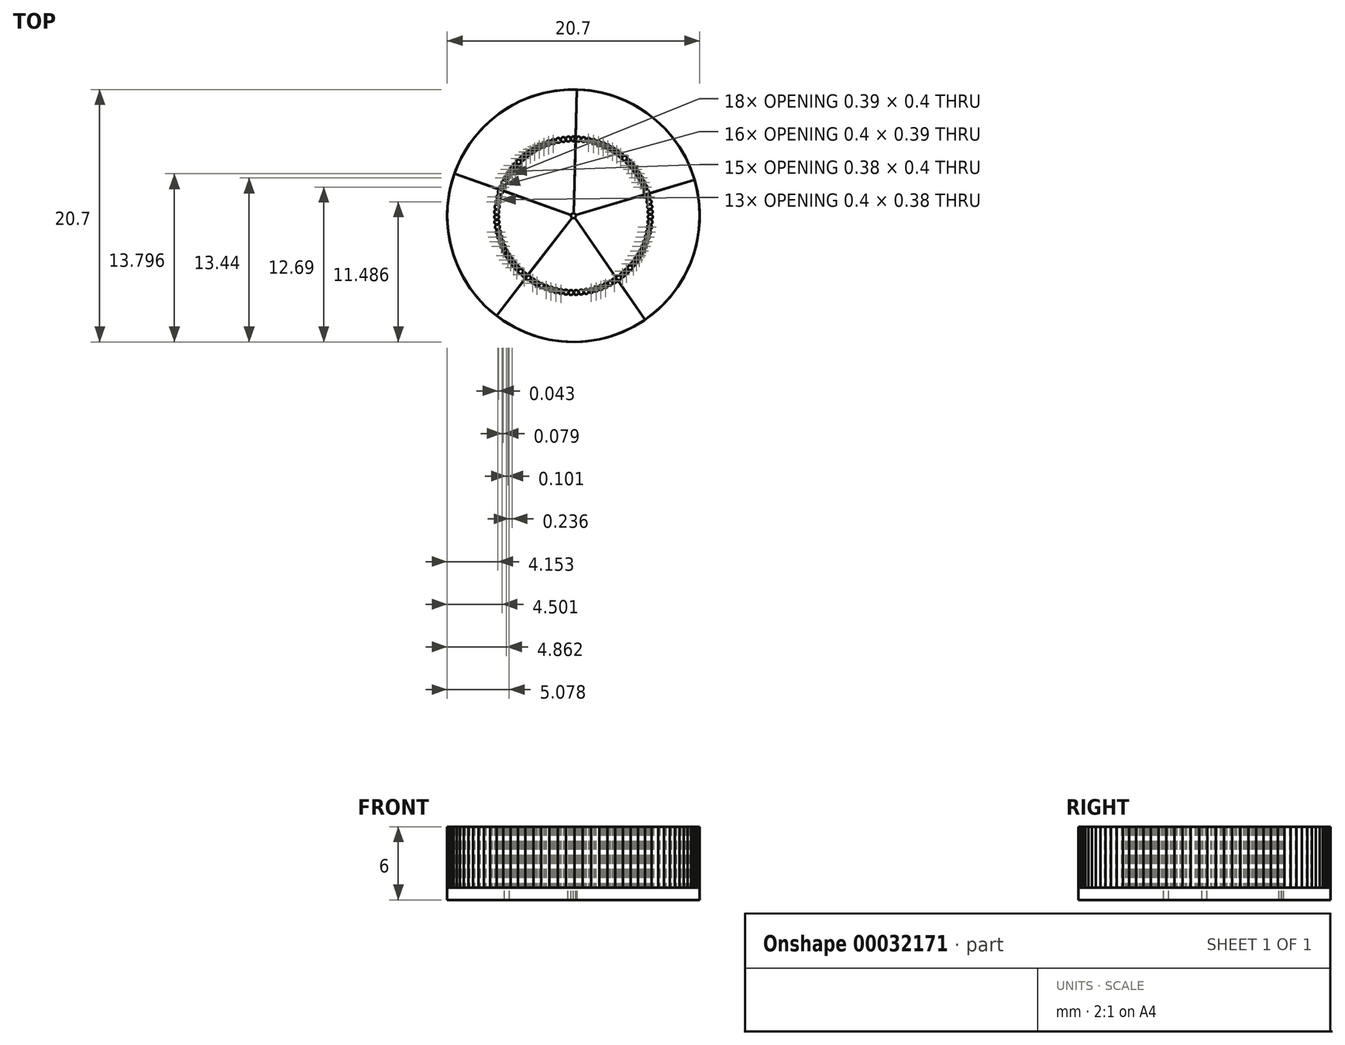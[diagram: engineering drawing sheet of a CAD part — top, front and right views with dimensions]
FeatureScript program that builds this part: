
annotation { "Feature Type Name" : "Feature", "Feature Type Description" : "" }
export const myFeature = defineFeature(function(context is Context, id is Id, definition is map)
    precondition{}
    {
        {
            var Q0;
            Q0=qCreatedBy(makeId("Top.planeOp"),FACE);
            var sketch = newSketch(context, id + "F0", { "sketchPlane" : qUnion([Q0])});
            skCircle(sketch, "E0", {"center": v(0, 0) * mm, "radius": 32.06 * mm});
            skCircle(sketch, "E1", {"center": v(0, 0) * mm, "radius": 0.2 * mm});
            skCircle(sketch, "E2", {"center": v(0, 0) * mm, "radius": 10.35 * mm});
            skCircle(sketch, "E3", {"center": v(0, 6.3) * mm, "radius": 0.2 * mm});
            skCircle(sketch, "E4", {"center": v(5.46, -3.15) * mm, "radius": 0.2 * mm});
            skCircle(sketch, "E5", {"center": v(-5.46, -3.15) * mm, "radius": 0.2 * mm});
            skLineSegment(sketch, "E6", {"start": v(0.26, 9.75) * mm, "end": v(0.26, 9.74) * mm});
            skLineSegment(sketch, "E7", {"start": v(0.26, 9.74) * mm, "end": v(0.26, 9.74) * mm});
            skLineSegment(sketch, "E8", {"start": v(0.26, 9.74) * mm, "end": v(0.26, 9.73) * mm});
            skLineSegment(sketch, "E9", {"start": v(0.26, 9.73) * mm, "end": v(0.25, 9.73) * mm});
            skLineSegment(sketch, "E10", {"start": v(0.25, 9.73) * mm, "end": v(0.25, 9.72) * mm});
            skLineSegment(sketch, "E11", {"start": v(0.25, 9.72) * mm, "end": v(0.25, 9.72) * mm});
            skLineSegment(sketch, "E12", {"start": v(0.25, 9.72) * mm, "end": v(0.25, 9.71) * mm});
            skLineSegment(sketch, "E13", {"start": v(0.25, 9.71) * mm, "end": v(0.24, 9.7) * mm});
            skLineSegment(sketch, "E14", {"start": v(0.24, 9.7) * mm, "end": v(0.24, 9.7) * mm});
            skLineSegment(sketch, "E15", {"start": v(0.24, 9.7) * mm, "end": v(0.24, 9.69) * mm});
            skLineSegment(sketch, "E16", {"start": v(0.24, 9.69) * mm, "end": v(0.23, 9.68) * mm});
            skLineSegment(sketch, "E17", {"start": v(0.23, 9.68) * mm, "end": v(0.23, 9.68) * mm});
            skLineSegment(sketch, "E18", {"start": v(0.23, 9.68) * mm, "end": v(0.23, 9.67) * mm});
            skLineSegment(sketch, "E19", {"start": v(0.23, 9.67) * mm, "end": v(0.23, 9.67) * mm});
            skLineSegment(sketch, "E20", {"start": v(0.23, 9.67) * mm, "end": v(0.22, 9.66) * mm});
            skLineSegment(sketch, "E21", {"start": v(0.22, 9.66) * mm, "end": v(0.22, 9.66) * mm});
            skLineSegment(sketch, "E22", {"start": v(0.22, 9.66) * mm, "end": v(0.22, 9.65) * mm});
            skLineSegment(sketch, "E23", {"start": v(0.22, 9.65) * mm, "end": v(0.22, 9.65) * mm});
            skLineSegment(sketch, "E24", {"start": v(0.22, 9.65) * mm, "end": v(0.22, 9.64) * mm});
            skLineSegment(sketch, "E25", {"start": v(0.22, 9.64) * mm, "end": v(0.21, 9.64) * mm});
            skLineSegment(sketch, "E26", {"start": v(0.21, 9.64) * mm, "end": v(0.21, 9.64) * mm});
            skLineSegment(sketch, "E27", {"start": v(0.21, 9.64) * mm, "end": v(0.21, 9.63) * mm});
            skLineSegment(sketch, "E28", {"start": v(0.21, 9.63) * mm, "end": v(0.2, 9.63) * mm});
            skLineSegment(sketch, "E29", {"start": v(0.2, 9.63) * mm, "end": v(0.2, 9.62) * mm});
            skLineSegment(sketch, "E30", {"start": v(0.2, 9.62) * mm, "end": v(0.2, 9.62) * mm});
            skLineSegment(sketch, "E31", {"start": v(0.2, 9.62) * mm, "end": v(0.2, 9.61) * mm});
            skLineSegment(sketch, "E32", {"start": v(0.2, 9.61) * mm, "end": v(0.2, 9.6) * mm});
            skLineSegment(sketch, "E33", {"start": v(0.2, 9.6) * mm, "end": v(0.2, 9.6) * mm});
            skLineSegment(sketch, "E34", {"start": v(0.2, 9.6) * mm, "end": v(0.2, 9.59) * mm});
            skLineSegment(sketch, "E35", {"start": v(0.2, 9.59) * mm, "end": v(0.2, 9.58) * mm});
            skLineSegment(sketch, "E36", {"start": v(0.2, 9.58) * mm, "end": v(0.19, 9.58) * mm});
            skLineSegment(sketch, "E37", {"start": v(0.19, 9.58) * mm, "end": v(0.19, 9.57) * mm});
            skLineSegment(sketch, "E38", {"start": v(0.19, 9.57) * mm, "end": v(0.18, 9.57) * mm});
            skLineSegment(sketch, "E39", {"start": v(0.18, 9.57) * mm, "end": v(0.18, 9.56) * mm});
            skLineSegment(sketch, "E40", {"start": v(0.18, 9.56) * mm, "end": v(0.18, 9.56) * mm});
            skLineSegment(sketch, "E41", {"start": v(0.18, 9.56) * mm, "end": v(0.18, 9.55) * mm});
            skLineSegment(sketch, "E42", {"start": v(0.18, 9.55) * mm, "end": v(0.18, 9.55) * mm});
            skLineSegment(sketch, "E43", {"start": v(0.18, 9.55) * mm, "end": v(0.17, 9.54) * mm});
            skLineSegment(sketch, "E44", {"start": v(0.17, 9.54) * mm, "end": v(0.17, 9.54) * mm});
            skLineSegment(sketch, "E45", {"start": v(0.17, 9.54) * mm, "end": v(0.17, 9.53) * mm});
            skLineSegment(sketch, "E46", {"start": v(0.17, 9.53) * mm, "end": v(0.17, 9.53) * mm});
            skLineSegment(sketch, "E47", {"start": v(0.17, 9.53) * mm, "end": v(0.17, 9.52) * mm});
            skLineSegment(sketch, "E48", {"start": v(0.17, 9.52) * mm, "end": v(0.16, 9.52) * mm});
            skLineSegment(sketch, "E49", {"start": v(0.16, 9.52) * mm, "end": v(0.16, 9.51) * mm});
            skLineSegment(sketch, "E50", {"start": v(0.16, 9.51) * mm, "end": v(0.16, 9.51) * mm});
            skLineSegment(sketch, "E51", {"start": v(0.16, 9.51) * mm, "end": v(0.16, 9.5) * mm});
            skLineSegment(sketch, "E52", {"start": v(0.16, 9.5) * mm, "end": v(0.16, 9.5) * mm});
            skLineSegment(sketch, "E53", {"start": v(0.16, 9.5) * mm, "end": v(0.15, 9.5) * mm});
            skLineSegment(sketch, "E54", {"start": v(0.15, 9.5) * mm, "end": v(0.15, 9.49) * mm});
            skLineSegment(sketch, "E55", {"start": v(0.15, 9.49) * mm, "end": v(0.15, 9.48) * mm});
            skLineSegment(sketch, "E56", {"start": v(0.15, 9.48) * mm, "end": v(0.15, 9.48) * mm});
            skLineSegment(sketch, "E57", {"start": v(0.15, 9.48) * mm, "end": v(0.15, 9.47) * mm});
            skLineSegment(sketch, "E58", {"start": v(0.15, 9.47) * mm, "end": v(0.15, 9.47) * mm});
            skLineSegment(sketch, "E59", {"start": v(0.15, 9.47) * mm, "end": v(0.14, 9.47) * mm});
            skLineSegment(sketch, "E60", {"start": v(0.14, 9.47) * mm, "end": v(0.14, 9.46) * mm});
            skLineSegment(sketch, "E61", {"start": v(0.14, 9.46) * mm, "end": v(0.14, 9.46) * mm});
            skLineSegment(sketch, "E62", {"start": v(0.14, 9.46) * mm, "end": v(0.14, 9.45) * mm});
            skLineSegment(sketch, "E63", {"start": v(0.14, 9.45) * mm, "end": v(0.14, 9.45) * mm});
            skLineSegment(sketch, "E64", {"start": v(0.14, 9.45) * mm, "end": v(0.14, 9.44) * mm});
            skLineSegment(sketch, "E65", {"start": v(0.14, 9.44) * mm, "end": v(0.13, 9.44) * mm});
            skLineSegment(sketch, "E66", {"start": v(0.13, 9.44) * mm, "end": v(0.13, 9.43) * mm});
            skLineSegment(sketch, "E67", {"start": v(0.13, 9.43) * mm, "end": v(0.13, 9.43) * mm});
            skLineSegment(sketch, "E68", {"start": v(0.13, 9.43) * mm, "end": v(0.13, 9.42) * mm});
            skLineSegment(sketch, "E69", {"start": v(0.13, 9.42) * mm, "end": v(0.13, 9.42) * mm});
            skLineSegment(sketch, "E70", {"start": v(0.13, 9.42) * mm, "end": v(0.12, 9.41) * mm});
            skLineSegment(sketch, "E71", {"start": v(0.12, 9.41) * mm, "end": v(0.12, 9.4) * mm});
            skLineSegment(sketch, "E72", {"start": v(0.12, 9.4) * mm, "end": v(0.12, 9.4) * mm});
            skLineSegment(sketch, "E73", {"start": v(0.12, 9.4) * mm, "end": v(0.12, 9.39) * mm});
            skLineSegment(sketch, "E74", {"start": v(0.12, 9.39) * mm, "end": v(0.12, 9.38) * mm});
            skLineSegment(sketch, "E75", {"start": v(0.12, 9.38) * mm, "end": v(0.11, 9.38) * mm});
            skLineSegment(sketch, "E76", {"start": v(0.11, 9.38) * mm, "end": v(0.11, 9.38) * mm});
            skLineSegment(sketch, "E77", {"start": v(0.11, 9.38) * mm, "end": v(0.11, 9.37) * mm});
            skLineSegment(sketch, "E78", {"start": v(0.11, 9.37) * mm, "end": v(0.1, 9.37) * mm});
            skLineSegment(sketch, "E79", {"start": v(0.1, 9.37) * mm, "end": v(0.1, 9.36) * mm});
            skLineSegment(sketch, "E80", {"start": v(0.1, 9.36) * mm, "end": v(0.1, 9.36) * mm});
            skLineSegment(sketch, "E81", {"start": v(0.1, 9.36) * mm, "end": v(0.1, 9.35) * mm});
            skLineSegment(sketch, "E82", {"start": v(0.1, 9.35) * mm, "end": v(0.1, 9.35) * mm});
            skLineSegment(sketch, "E83", {"start": v(0.1, 9.35) * mm, "end": v(0.1, 9.34) * mm});
            skLineSegment(sketch, "E84", {"start": v(0.1, 9.34) * mm, "end": v(0.1, 9.34) * mm});
            skLineSegment(sketch, "E85", {"start": v(0.1, 9.34) * mm, "end": v(0.1, 9.33) * mm});
            skLineSegment(sketch, "E86", {"start": v(0.1, 9.33) * mm, "end": v(0.1, 9.33) * mm});
            skLineSegment(sketch, "E87", {"start": v(0.1, 9.33) * mm, "end": v(0.1, 9.32) * mm});
            skLineSegment(sketch, "E88", {"start": v(0.1, 9.32) * mm, "end": v(0.1, 9.32) * mm});
            skLineSegment(sketch, "E89", {"start": v(0.1, 9.32) * mm, "end": v(0.09, 9.31) * mm});
            skLineSegment(sketch, "E90", {"start": v(0.09, 9.31) * mm, "end": v(0.09, 9.3) * mm});
            skLineSegment(sketch, "E91", {"start": v(0.09, 9.3) * mm, "end": v(0.09, 9.3) * mm});
            skLineSegment(sketch, "E92", {"start": v(0.09, 9.3) * mm, "end": v(0, 9.3) * mm});
            skLineSegment(sketch, "E93", {"start": v(0, 9.3) * mm, "end": v(-0.09, 9.3) * mm});
            skLineSegment(sketch, "E94", {"start": v(-0.09, 9.3) * mm, "end": v(-0.09, 9.3) * mm});
            skLineSegment(sketch, "E95", {"start": v(-0.09, 9.3) * mm, "end": v(-0.09, 9.31) * mm});
            skLineSegment(sketch, "E96", {"start": v(-0.09, 9.31) * mm, "end": v(-0.1, 9.32) * mm});
            skLineSegment(sketch, "E97", {"start": v(-0.1, 9.32) * mm, "end": v(-0.1, 9.32) * mm});
            skLineSegment(sketch, "E98", {"start": v(-0.1, 9.32) * mm, "end": v(-0.1, 9.33) * mm});
            skLineSegment(sketch, "E99", {"start": v(-0.1, 9.33) * mm, "end": v(-0.1, 9.33) * mm});
            skLineSegment(sketch, "E100", {"start": v(-0.1, 9.33) * mm, "end": v(-0.1, 9.34) * mm});
            skLineSegment(sketch, "E101", {"start": v(-0.1, 9.34) * mm, "end": v(-0.1, 9.34) * mm});
            skLineSegment(sketch, "E102", {"start": v(-0.1, 9.34) * mm, "end": v(-0.1, 9.35) * mm});
            skLineSegment(sketch, "E103", {"start": v(-0.1, 9.35) * mm, "end": v(-0.1, 9.35) * mm});
            skLineSegment(sketch, "E104", {"start": v(-0.1, 9.35) * mm, "end": v(-0.1, 9.36) * mm});
            skLineSegment(sketch, "E105", {"start": v(-0.1, 9.36) * mm, "end": v(-0.1, 9.36) * mm});
            skLineSegment(sketch, "E106", {"start": v(-0.1, 9.36) * mm, "end": v(-0.1, 9.37) * mm});
            skLineSegment(sketch, "E107", {"start": v(-0.1, 9.37) * mm, "end": v(-0.11, 9.37) * mm});
            skLineSegment(sketch, "E108", {"start": v(-0.11, 9.37) * mm, "end": v(-0.11, 9.38) * mm});
            skLineSegment(sketch, "E109", {"start": v(-0.11, 9.38) * mm, "end": v(-0.11, 9.38) * mm});
            skLineSegment(sketch, "E110", {"start": v(-0.11, 9.38) * mm, "end": v(-0.12, 9.38) * mm});
            skLineSegment(sketch, "E111", {"start": v(-0.12, 9.38) * mm, "end": v(-0.12, 9.39) * mm});
            skLineSegment(sketch, "E112", {"start": v(-0.12, 9.39) * mm, "end": v(-0.12, 9.4) * mm});
            skLineSegment(sketch, "E113", {"start": v(-0.12, 9.4) * mm, "end": v(-0.12, 9.4) * mm});
            skLineSegment(sketch, "E114", {"start": v(-0.12, 9.4) * mm, "end": v(-0.12, 9.41) * mm});
            skLineSegment(sketch, "E115", {"start": v(-0.12, 9.41) * mm, "end": v(-0.13, 9.42) * mm});
            skLineSegment(sketch, "E116", {"start": v(-0.13, 9.42) * mm, "end": v(-0.13, 9.42) * mm});
            skLineSegment(sketch, "E117", {"start": v(-0.13, 9.42) * mm, "end": v(-0.13, 9.43) * mm});
            skLineSegment(sketch, "E118", {"start": v(-0.13, 9.43) * mm, "end": v(-0.13, 9.43) * mm});
            skLineSegment(sketch, "E119", {"start": v(-0.13, 9.43) * mm, "end": v(-0.13, 9.44) * mm});
            skLineSegment(sketch, "E120", {"start": v(-0.13, 9.44) * mm, "end": v(-0.14, 9.44) * mm});
            skLineSegment(sketch, "E121", {"start": v(-0.14, 9.44) * mm, "end": v(-0.14, 9.45) * mm});
            skLineSegment(sketch, "E122", {"start": v(-0.14, 9.45) * mm, "end": v(-0.14, 9.45) * mm});
            skLineSegment(sketch, "E123", {"start": v(-0.14, 9.45) * mm, "end": v(-0.14, 9.46) * mm});
            skLineSegment(sketch, "E124", {"start": v(-0.14, 9.46) * mm, "end": v(-0.14, 9.46) * mm});
            skLineSegment(sketch, "E125", {"start": v(-0.14, 9.46) * mm, "end": v(-0.14, 9.47) * mm});
            skLineSegment(sketch, "E126", {"start": v(-0.14, 9.47) * mm, "end": v(-0.15, 9.47) * mm});
            skLineSegment(sketch, "E127", {"start": v(-0.15, 9.47) * mm, "end": v(-0.15, 9.47) * mm});
            skLineSegment(sketch, "E128", {"start": v(-0.15, 9.47) * mm, "end": v(-0.15, 9.48) * mm});
            skLineSegment(sketch, "E129", {"start": v(-0.15, 9.48) * mm, "end": v(-0.15, 9.48) * mm});
            skLineSegment(sketch, "E130", {"start": v(-0.15, 9.48) * mm, "end": v(-0.15, 9.49) * mm});
            skLineSegment(sketch, "E131", {"start": v(-0.15, 9.49) * mm, "end": v(-0.15, 9.5) * mm});
            skLineSegment(sketch, "E132", {"start": v(-0.15, 9.5) * mm, "end": v(-0.16, 9.5) * mm});
            skLineSegment(sketch, "E133", {"start": v(-0.16, 9.5) * mm, "end": v(-0.16, 9.5) * mm});
            skLineSegment(sketch, "E134", {"start": v(-0.16, 9.5) * mm, "end": v(-0.16, 9.51) * mm});
            skLineSegment(sketch, "E135", {"start": v(-0.16, 9.51) * mm, "end": v(-0.16, 9.51) * mm});
            skLineSegment(sketch, "E136", {"start": v(-0.16, 9.51) * mm, "end": v(-0.16, 9.52) * mm});
            skLineSegment(sketch, "E137", {"start": v(-0.16, 9.52) * mm, "end": v(-0.17, 9.52) * mm});
            skLineSegment(sketch, "E138", {"start": v(-0.17, 9.52) * mm, "end": v(-0.17, 9.53) * mm});
            skLineSegment(sketch, "E139", {"start": v(-0.17, 9.53) * mm, "end": v(-0.17, 9.53) * mm});
            skLineSegment(sketch, "E140", {"start": v(-0.17, 9.53) * mm, "end": v(-0.17, 9.54) * mm});
            skLineSegment(sketch, "E141", {"start": v(-0.17, 9.54) * mm, "end": v(-0.17, 9.54) * mm});
            skLineSegment(sketch, "E142", {"start": v(-0.17, 9.54) * mm, "end": v(-0.18, 9.55) * mm});
            skLineSegment(sketch, "E143", {"start": v(-0.18, 9.55) * mm, "end": v(-0.18, 9.55) * mm});
            skLineSegment(sketch, "E144", {"start": v(-0.18, 9.55) * mm, "end": v(-0.18, 9.56) * mm});
            skLineSegment(sketch, "E145", {"start": v(-0.18, 9.56) * mm, "end": v(-0.18, 9.56) * mm});
            skLineSegment(sketch, "E146", {"start": v(-0.18, 9.56) * mm, "end": v(-0.18, 9.57) * mm});
            skLineSegment(sketch, "E147", {"start": v(-0.18, 9.57) * mm, "end": v(-0.19, 9.57) * mm});
            skLineSegment(sketch, "E148", {"start": v(-0.19, 9.57) * mm, "end": v(-0.19, 9.58) * mm});
            skLineSegment(sketch, "E149", {"start": v(-0.19, 9.58) * mm, "end": v(-0.2, 9.58) * mm});
            skLineSegment(sketch, "E150", {"start": v(-0.2, 9.58) * mm, "end": v(-0.2, 9.59) * mm});
            skLineSegment(sketch, "E151", {"start": v(-0.2, 9.59) * mm, "end": v(-0.2, 9.6) * mm});
            skLineSegment(sketch, "E152", {"start": v(-0.2, 9.6) * mm, "end": v(-0.2, 9.6) * mm});
            skLineSegment(sketch, "E153", {"start": v(-0.2, 9.6) * mm, "end": v(-0.2, 9.61) * mm});
            skLineSegment(sketch, "E154", {"start": v(-0.2, 9.61) * mm, "end": v(-0.2, 9.62) * mm});
            skLineSegment(sketch, "E155", {"start": v(-0.2, 9.62) * mm, "end": v(-0.2, 9.62) * mm});
            skLineSegment(sketch, "E156", {"start": v(-0.2, 9.62) * mm, "end": v(-0.2, 9.63) * mm});
            skLineSegment(sketch, "E157", {"start": v(-0.2, 9.63) * mm, "end": v(-0.21, 9.63) * mm});
            skLineSegment(sketch, "E158", {"start": v(-0.21, 9.63) * mm, "end": v(-0.21, 9.64) * mm});
            skLineSegment(sketch, "E159", {"start": v(-0.21, 9.64) * mm, "end": v(-0.21, 9.64) * mm});
            skLineSegment(sketch, "E160", {"start": v(-0.21, 9.64) * mm, "end": v(-0.22, 9.64) * mm});
            skLineSegment(sketch, "E161", {"start": v(-0.22, 9.64) * mm, "end": v(-0.22, 9.65) * mm});
            skLineSegment(sketch, "E162", {"start": v(-0.22, 9.65) * mm, "end": v(-0.22, 9.65) * mm});
            skLineSegment(sketch, "E163", {"start": v(-0.22, 9.65) * mm, "end": v(-0.22, 9.66) * mm});
            skLineSegment(sketch, "E164", {"start": v(-0.22, 9.66) * mm, "end": v(-0.22, 9.66) * mm});
            skLineSegment(sketch, "E165", {"start": v(-0.22, 9.66) * mm, "end": v(-0.23, 9.67) * mm});
            skLineSegment(sketch, "E166", {"start": v(-0.23, 9.67) * mm, "end": v(-0.23, 9.67) * mm});
            skLineSegment(sketch, "E167", {"start": v(-0.23, 9.67) * mm, "end": v(-0.23, 9.68) * mm});
            skLineSegment(sketch, "E168", {"start": v(-0.23, 9.68) * mm, "end": v(-0.23, 9.68) * mm});
            skLineSegment(sketch, "E169", {"start": v(-0.23, 9.68) * mm, "end": v(-0.24, 9.69) * mm});
            skLineSegment(sketch, "E170", {"start": v(-0.24, 9.69) * mm, "end": v(-0.24, 9.7) * mm});
            skLineSegment(sketch, "E171", {"start": v(-0.24, 9.7) * mm, "end": v(-0.24, 9.7) * mm});
            skLineSegment(sketch, "E172", {"start": v(-0.24, 9.7) * mm, "end": v(-0.25, 9.71) * mm});
            skLineSegment(sketch, "E173", {"start": v(-0.25, 9.71) * mm, "end": v(-0.25, 9.72) * mm});
            skLineSegment(sketch, "E174", {"start": v(-0.25, 9.72) * mm, "end": v(-0.25, 9.72) * mm});
            skLineSegment(sketch, "E175", {"start": v(-0.25, 9.72) * mm, "end": v(-0.25, 9.73) * mm});
            skLineSegment(sketch, "E176", {"start": v(-0.25, 9.73) * mm, "end": v(-0.26, 9.73) * mm});
            skLineSegment(sketch, "E177", {"start": v(-0.26, 9.73) * mm, "end": v(-0.26, 9.74) * mm});
            skLineSegment(sketch, "E178", {"start": v(-0.26, 9.74) * mm, "end": v(-0.26, 9.74) * mm});
            skLineSegment(sketch, "E179", {"start": v(-0.26, 9.74) * mm, "end": v(-0.26, 9.75) * mm});
            skLineSegment(sketch, "E180", {"start": v(-0.26, 9.75) * mm, "end": v(-0.38, 9.74) * mm});
            skLineSegment(sketch, "E181", {"start": v(-0.38, 9.74) * mm, "end": v(-0.38, 9.74) * mm});
            skLineSegment(sketch, "E182", {"start": v(-0.38, 9.74) * mm, "end": v(-0.39, 9.73) * mm});
            skLineSegment(sketch, "E183", {"start": v(-0.39, 9.73) * mm, "end": v(-0.39, 9.73) * mm});
            skLineSegment(sketch, "E184", {"start": v(-0.39, 9.73) * mm, "end": v(-0.39, 9.72) * mm});
            skLineSegment(sketch, "E185", {"start": v(-0.39, 9.72) * mm, "end": v(-0.4, 9.72) * mm});
            skLineSegment(sketch, "E186", {"start": v(-0.4, 9.72) * mm, "end": v(-0.4, 9.72) * mm});
            skLineSegment(sketch, "E187", {"start": v(-0.4, 9.72) * mm, "end": v(-0.4, 9.71) * mm});
            skLineSegment(sketch, "E188", {"start": v(-0.4, 9.71) * mm, "end": v(-0.4, 9.7) * mm});
            skLineSegment(sketch, "E189", {"start": v(-0.4, 9.7) * mm, "end": v(-0.4, 9.7) * mm});
            skLineSegment(sketch, "E190", {"start": v(-0.4, 9.7) * mm, "end": v(-0.4, 9.69) * mm});
            skLineSegment(sketch, "E191", {"start": v(-0.4, 9.69) * mm, "end": v(-0.4, 9.68) * mm});
            skLineSegment(sketch, "E192", {"start": v(-0.4, 9.68) * mm, "end": v(-0.4, 9.68) * mm});
            skLineSegment(sketch, "E193", {"start": v(-0.4, 9.68) * mm, "end": v(-0.4, 9.67) * mm});
            skLineSegment(sketch, "E194", {"start": v(-0.4, 9.67) * mm, "end": v(-0.4, 9.67) * mm});
            skLineSegment(sketch, "E195", {"start": v(-0.4, 9.67) * mm, "end": v(-0.41, 9.66) * mm});
            skLineSegment(sketch, "E196", {"start": v(-0.41, 9.66) * mm, "end": v(-0.41, 9.66) * mm});
            skLineSegment(sketch, "E197", {"start": v(-0.41, 9.66) * mm, "end": v(-0.42, 9.65) * mm});
            skLineSegment(sketch, "E198", {"start": v(-0.42, 9.65) * mm, "end": v(-0.42, 9.65) * mm});
            skLineSegment(sketch, "E199", {"start": v(-0.42, 9.65) * mm, "end": v(-0.42, 9.64) * mm});
            skLineSegment(sketch, "E200", {"start": v(-0.42, 9.64) * mm, "end": v(-0.42, 9.64) * mm});
            skLineSegment(sketch, "E201", {"start": v(-0.42, 9.64) * mm, "end": v(-0.42, 9.63) * mm});
            skLineSegment(sketch, "E202", {"start": v(-0.42, 9.63) * mm, "end": v(-0.42, 9.63) * mm});
            skLineSegment(sketch, "E203", {"start": v(-0.42, 9.63) * mm, "end": v(-0.43, 9.62) * mm});
            skLineSegment(sketch, "E204", {"start": v(-0.43, 9.62) * mm, "end": v(-0.43, 9.62) * mm});
            skLineSegment(sketch, "E205", {"start": v(-0.43, 9.62) * mm, "end": v(-0.43, 9.61) * mm});
            skLineSegment(sketch, "E206", {"start": v(-0.43, 9.61) * mm, "end": v(-0.43, 9.6) * mm});
            skLineSegment(sketch, "E207", {"start": v(-0.43, 9.6) * mm, "end": v(-0.43, 9.6) * mm});
            skLineSegment(sketch, "E208", {"start": v(-0.43, 9.6) * mm, "end": v(-0.44, 9.6) * mm});
            skLineSegment(sketch, "E209", {"start": v(-0.44, 9.6) * mm, "end": v(-0.44, 9.6) * mm});
            skLineSegment(sketch, "E210", {"start": v(-0.44, 9.6) * mm, "end": v(-0.44, 9.59) * mm});
            skLineSegment(sketch, "E211", {"start": v(-0.44, 9.59) * mm, "end": v(-0.44, 9.58) * mm});
            skLineSegment(sketch, "E212", {"start": v(-0.44, 9.58) * mm, "end": v(-0.44, 9.58) * mm});
            skLineSegment(sketch, "E213", {"start": v(-0.44, 9.58) * mm, "end": v(-0.44, 9.57) * mm});
            skLineSegment(sketch, "E214", {"start": v(2.96, -0.58) * mm, "end": v(2.96, -0.58) * mm});
            skLineSegment(sketch, "E215", {"start": v(2.96, -0.58) * mm, "end": v(2.95, -0.58) * mm});
            skLineSegment(sketch, "E216", {"start": v(2.95, -0.58) * mm, "end": v(2.95, -0.58) * mm});
            skLineSegment(sketch, "E217", {"start": v(2.95, -0.58) * mm, "end": v(2.94, -0.57) * mm});
            skLineSegment(sketch, "E218", {"start": v(2.94, -0.57) * mm, "end": v(2.94, -0.57) * mm});
            skLineSegment(sketch, "E219", {"start": v(2.94, -0.57) * mm, "end": v(2.93, -0.57) * mm});
            skLineSegment(sketch, "E220", {"start": v(2.93, -0.57) * mm, "end": v(2.93, -0.57) * mm});
            skLineSegment(sketch, "E221", {"start": v(2.93, -0.57) * mm, "end": v(2.92, -0.56) * mm});
            skLineSegment(sketch, "E222", {"start": v(2.92, -0.56) * mm, "end": v(2.92, -0.56) * mm});
            skLineSegment(sketch, "E223", {"start": v(2.92, -0.56) * mm, "end": v(2.91, -0.56) * mm});
            skLineSegment(sketch, "E224", {"start": v(2.91, -0.56) * mm, "end": v(2.9, -0.56) * mm});
            skLineSegment(sketch, "E225", {"start": v(2.9, -0.56) * mm, "end": v(2.9, -0.56) * mm});
            skLineSegment(sketch, "E226", {"start": v(2.9, -0.56) * mm, "end": v(2.9, -0.55) * mm});
            skLineSegment(sketch, "E227", {"start": v(2.9, -0.55) * mm, "end": v(2.9, -0.55) * mm});
            skLineSegment(sketch, "E228", {"start": v(2.9, -0.55) * mm, "end": v(2.89, -0.55) * mm});
            skLineSegment(sketch, "E229", {"start": v(2.89, -0.55) * mm, "end": v(2.88, -0.55) * mm});
            skLineSegment(sketch, "E230", {"start": v(2.88, -0.55) * mm, "end": v(2.88, -0.55) * mm});
            skLineSegment(sketch, "E231", {"start": v(2.88, -0.55) * mm, "end": v(2.87, -0.55) * mm});
            skLineSegment(sketch, "E232", {"start": v(2.87, -0.55) * mm, "end": v(2.87, -0.55) * mm});
            skLineSegment(sketch, "E233", {"start": v(2.87, -0.55) * mm, "end": v(2.87, -0.54) * mm});
            skLineSegment(sketch, "E234", {"start": v(2.87, -0.54) * mm, "end": v(2.86, -0.54) * mm});
            skLineSegment(sketch, "E235", {"start": v(2.86, -0.54) * mm, "end": v(2.86, -0.54) * mm});
            skLineSegment(sketch, "E236", {"start": v(2.86, -0.54) * mm, "end": v(2.85, -0.54) * mm});
            skLineSegment(sketch, "E237", {"start": v(2.85, -0.54) * mm, "end": v(2.85, -0.54) * mm});
            skLineSegment(sketch, "E238", {"start": v(2.85, -0.54) * mm, "end": v(2.85, -0.53) * mm});
            skLineSegment(sketch, "E239", {"start": v(2.85, -0.53) * mm, "end": v(2.84, -0.53) * mm});
            skLineSegment(sketch, "E240", {"start": v(2.84, -0.53) * mm, "end": v(2.84, -0.53) * mm});
            skLineSegment(sketch, "E241", {"start": v(2.84, -0.53) * mm, "end": v(2.83, -0.53) * mm});
            skLineSegment(sketch, "E242", {"start": v(2.83, -0.53) * mm, "end": v(2.83, -0.53) * mm});
            skLineSegment(sketch, "E243", {"start": v(2.83, -0.53) * mm, "end": v(2.82, -0.52) * mm});
            skLineSegment(sketch, "E244", {"start": v(2.82, -0.52) * mm, "end": v(2.82, -0.52) * mm});
            skLineSegment(sketch, "E245", {"start": v(2.82, -0.52) * mm, "end": v(2.81, -0.51) * mm});
            skLineSegment(sketch, "E246", {"start": v(2.81, -0.51) * mm, "end": v(2.8, -0.5) * mm});
            skLineSegment(sketch, "E247", {"start": v(2.8, -0.5) * mm, "end": v(2.82, -0.43) * mm});
            skLineSegment(sketch, "E248", {"start": v(2.82, -0.43) * mm, "end": v(2.83, -0.36) * mm});
            skLineSegment(sketch, "E249", {"start": v(2.83, -0.36) * mm, "end": v(2.84, -0.35) * mm});
            skLineSegment(sketch, "E250", {"start": v(2.84, -0.35) * mm, "end": v(2.84, -0.35) * mm});
            skLineSegment(sketch, "E251", {"start": v(2.84, -0.35) * mm, "end": v(2.85, -0.35) * mm});
            skLineSegment(sketch, "E252", {"start": v(2.85, -0.35) * mm, "end": v(2.85, -0.35) * mm});
            skLineSegment(sketch, "E253", {"start": v(2.85, -0.35) * mm, "end": v(2.86, -0.35) * mm});
            skLineSegment(sketch, "E254", {"start": v(2.86, -0.35) * mm, "end": v(2.86, -0.34) * mm});
            skLineSegment(sketch, "E255", {"start": v(2.86, -0.34) * mm, "end": v(2.87, -0.34) * mm});
            skLineSegment(sketch, "E256", {"start": v(2.87, -0.34) * mm, "end": v(2.87, -0.34) * mm});
            skLineSegment(sketch, "E257", {"start": v(2.87, -0.34) * mm, "end": v(2.88, -0.34) * mm});
            skLineSegment(sketch, "E258", {"start": v(2.88, -0.34) * mm, "end": v(2.88, -0.34) * mm});
            skLineSegment(sketch, "E259", {"start": v(2.88, -0.34) * mm, "end": v(2.89, -0.34) * mm});
            skLineSegment(sketch, "E260", {"start": v(2.89, -0.34) * mm, "end": v(2.9, -0.34) * mm});
            skLineSegment(sketch, "E261", {"start": v(2.9, -0.34) * mm, "end": v(2.9, -0.34) * mm});
            skLineSegment(sketch, "E262", {"start": v(2.9, -0.34) * mm, "end": v(2.91, -0.34) * mm});
            skLineSegment(sketch, "E263", {"start": v(2.91, -0.34) * mm, "end": v(2.92, -0.34) * mm});
            skLineSegment(sketch, "E264", {"start": v(2.92, -0.34) * mm, "end": v(2.92, -0.34) * mm});
            skLineSegment(sketch, "E265", {"start": v(2.92, -0.34) * mm, "end": v(2.93, -0.34) * mm});
            skLineSegment(sketch, "E266", {"start": v(2.93, -0.34) * mm, "end": v(2.93, -0.34) * mm});
            skLineSegment(sketch, "E267", {"start": v(2.93, -0.34) * mm, "end": v(2.94, -0.34) * mm});
            skLineSegment(sketch, "E268", {"start": v(2.94, -0.34) * mm, "end": v(2.94, -0.34) * mm});
            skLineSegment(sketch, "E269", {"start": v(2.94, -0.34) * mm, "end": v(2.95, -0.34) * mm});
            skLineSegment(sketch, "E270", {"start": v(2.95, -0.34) * mm, "end": v(2.95, -0.34) * mm});
            skLineSegment(sketch, "E271", {"start": v(2.95, -0.34) * mm, "end": v(2.96, -0.34) * mm});
            skLineSegment(sketch, "E272", {"start": v(2.96, -0.34) * mm, "end": v(2.96, -0.34) * mm});
            skLineSegment(sketch, "E273", {"start": v(2.96, -0.34) * mm, "end": v(2.97, -0.34) * mm});
            skLineSegment(sketch, "E274", {"start": v(2.97, -0.34) * mm, "end": v(2.97, -0.33) * mm});
            skLineSegment(sketch, "E275", {"start": v(2.97, -0.33) * mm, "end": v(2.98, -0.33) * mm});
            skLineSegment(sketch, "E276", {"start": v(2.98, -0.33) * mm, "end": v(2.98, -0.33) * mm});
            skLineSegment(sketch, "E277", {"start": v(2.98, -0.33) * mm, "end": v(2.99, -0.33) * mm});
            skLineSegment(sketch, "E278", {"start": v(2.99, -0.33) * mm, "end": v(3, -0.33) * mm});
            skLineSegment(sketch, "E279", {"start": v(3, -0.33) * mm, "end": v(3, -0.33) * mm});
            skLineSegment(sketch, "E280", {"start": v(3, -0.33) * mm, "end": v(3.01, -0.33) * mm});
            skLineSegment(sketch, "E281", {"start": v(3.01, -0.33) * mm, "end": v(3.02, -0.33) * mm});
            skLineSegment(sketch, "E282", {"start": v(3.02, -0.33) * mm, "end": v(3.02, -0.33) * mm});
            skLineSegment(sketch, "E283", {"start": v(3.02, -0.33) * mm, "end": v(3.03, -0.33) * mm});
            skLineSegment(sketch, "E284", {"start": v(3.03, -0.33) * mm, "end": v(3.03, -0.33) * mm});
            skLineSegment(sketch, "E285", {"start": v(3.03, -0.33) * mm, "end": v(3.04, -0.32) * mm});
            skLineSegment(sketch, "E286", {"start": v(3.04, -0.32) * mm, "end": v(3.04, -0.32) * mm});
            skLineSegment(sketch, "E287", {"start": v(3.04, -0.32) * mm, "end": v(3.05, -0.32) * mm});
            skLineSegment(sketch, "E288", {"start": v(3.05, -0.32) * mm, "end": v(3.05, -0.32) * mm});
            skLineSegment(sketch, "E289", {"start": v(3.05, -0.32) * mm, "end": v(3.06, -0.32) * mm});
            skLineSegment(sketch, "E290", {"start": v(3.06, -0.32) * mm, "end": v(3.06, -0.32) * mm});
            skLineSegment(sketch, "E291", {"start": v(3.06, -0.32) * mm, "end": v(3.07, -0.32) * mm});
            skLineSegment(sketch, "E292", {"start": v(3.07, -0.32) * mm, "end": v(3.07, -0.32) * mm});
            skLineSegment(sketch, "E293", {"start": v(3.07, -0.32) * mm, "end": v(3.08, -0.32) * mm});
            skLineSegment(sketch, "E294", {"start": v(3.08, -0.32) * mm, "end": v(3.08, -0.31) * mm});
            skLineSegment(sketch, "E295", {"start": v(3.08, -0.31) * mm, "end": v(3.09, -0.31) * mm});
            skLineSegment(sketch, "E296", {"start": v(3.09, -0.31) * mm, "end": v(3.1, -0.31) * mm});
            skLineSegment(sketch, "E297", {"start": v(3.1, -0.31) * mm, "end": v(3.1, -0.31) * mm});
            skLineSegment(sketch, "E298", {"start": v(3.1, -0.31) * mm, "end": v(3.1, -0.3) * mm});
            skLineSegment(sketch, "E299", {"start": v(3.1, -0.3) * mm, "end": v(3.1, -0.3) * mm});
            skLineSegment(sketch, "E300", {"start": v(3.1, -0.3) * mm, "end": v(3.11, -0.3) * mm});
            skLineSegment(sketch, "E301", {"start": v(3.11, -0.3) * mm, "end": v(3.12, -0.3) * mm});
            skLineSegment(sketch, "E302", {"start": v(3.12, -0.3) * mm, "end": v(3.12, -0.3) * mm});
            skLineSegment(sketch, "E303", {"start": v(3.12, -0.3) * mm, "end": v(3.13, -0.3) * mm});
            skLineSegment(sketch, "E304", {"start": v(3.13, -0.3) * mm, "end": v(3.13, -0.3) * mm});
            skLineSegment(sketch, "E305", {"start": v(3.13, -0.3) * mm, "end": v(3.14, -0.3) * mm});
            skLineSegment(sketch, "E306", {"start": v(3.14, -0.3) * mm, "end": v(3.14, -0.3) * mm});
            skLineSegment(sketch, "E307", {"start": v(3.14, -0.3) * mm, "end": v(3.15, -0.3) * mm});
            skLineSegment(sketch, "E308", {"start": v(3.15, -0.3) * mm, "end": v(3.15, -0.3) * mm});
            skLineSegment(sketch, "E309", {"start": v(3.15, -0.3) * mm, "end": v(3.16, -0.3) * mm});
            skLineSegment(sketch, "E310", {"start": v(3.16, -0.3) * mm, "end": v(3.16, -0.3) * mm});
            skLineSegment(sketch, "E311", {"start": v(3.16, -0.3) * mm, "end": v(3.17, -0.29) * mm});
            skLineSegment(sketch, "E312", {"start": v(3.17, -0.29) * mm, "end": v(3.17, -0.29) * mm});
            skLineSegment(sketch, "E313", {"start": v(3.17, -0.29) * mm, "end": v(3.18, -0.29) * mm});
            skLineSegment(sketch, "E314", {"start": v(3.18, -0.29) * mm, "end": v(3.18, -0.28) * mm});
            skLineSegment(sketch, "E315", {"start": v(3.18, -0.28) * mm, "end": v(3.19, -0.28) * mm});
            skLineSegment(sketch, "E316", {"start": v(3.19, -0.28) * mm, "end": v(3.2, -0.28) * mm});
            skLineSegment(sketch, "E317", {"start": v(3.2, -0.28) * mm, "end": v(3.2, -0.28) * mm});
            skLineSegment(sketch, "E318", {"start": v(3.2, -0.28) * mm, "end": v(3.21, -0.27) * mm});
            skLineSegment(sketch, "E319", {"start": v(3.21, -0.27) * mm, "end": v(3.22, -0.27) * mm});
            skLineSegment(sketch, "E320", {"start": v(3.22, -0.27) * mm, "end": v(3.22, -0.27) * mm});
            skLineSegment(sketch, "E321", {"start": v(3.22, -0.27) * mm, "end": v(3.23, -0.27) * mm});
            skLineSegment(sketch, "E322", {"start": v(3.23, -0.27) * mm, "end": v(3.23, -0.27) * mm});
            skLineSegment(sketch, "E323", {"start": v(3.23, -0.27) * mm, "end": v(3.24, -0.26) * mm});
            skLineSegment(sketch, "E324", {"start": v(3.24, -0.26) * mm, "end": v(3.24, -0.26) * mm});
            skLineSegment(sketch, "E325", {"start": v(3.24, -0.26) * mm, "end": v(3.25, -0.26) * mm});
            skLineSegment(sketch, "E326", {"start": v(3.25, -0.26) * mm, "end": v(3.25, -0.26) * mm});
            skLineSegment(sketch, "E327", {"start": v(3.25, -0.26) * mm, "end": v(3.26, -0.26) * mm});
            skLineSegment(sketch, "E328", {"start": v(3.26, -0.26) * mm, "end": v(3.26, -0.25) * mm});
            skLineSegment(sketch, "E329", {"start": v(3.26, -0.25) * mm, "end": v(3.27, -0.25) * mm});
            skLineSegment(sketch, "E330", {"start": v(3.27, -0.25) * mm, "end": v(3.27, -0.25) * mm});
            skLineSegment(sketch, "E331", {"start": v(3.27, -0.25) * mm, "end": v(3.28, -0.25) * mm});
            skLineSegment(sketch, "E332", {"start": v(3.28, -0.25) * mm, "end": v(3.28, -0.25) * mm});
            skLineSegment(sketch, "E333", {"start": v(3.28, -0.25) * mm, "end": v(3.29, -0.24) * mm});
            skLineSegment(sketch, "E334", {"start": v(3.29, -0.24) * mm, "end": v(3.3, -0.24) * mm});
            skLineSegment(sketch, "E335", {"start": v(3.3, -0.24) * mm, "end": v(3.3, -0.1) * mm});
            skLineSegment(sketch, "E336", {"start": v(3.3, -0.1) * mm, "end": v(3.3, -0.1) * mm});
            skLineSegment(sketch, "E337", {"start": v(3.3, -0.1) * mm, "end": v(3.29, -0.09) * mm});
            skLineSegment(sketch, "E338", {"start": v(3.29, -0.09) * mm, "end": v(3.29, -0.09) * mm});
            skLineSegment(sketch, "E339", {"start": v(3.29, -0.09) * mm, "end": v(3.28, -0.08) * mm});
            skLineSegment(sketch, "E340", {"start": v(3.28, -0.08) * mm, "end": v(3.28, -0.08) * mm});
            skLineSegment(sketch, "E341", {"start": v(3.28, -0.08) * mm, "end": v(3.27, -0.08) * mm});
            skLineSegment(sketch, "E342", {"start": v(3.27, -0.08) * mm, "end": v(3.27, -0.08) * mm});
            skLineSegment(sketch, "E343", {"start": v(3.27, -0.08) * mm, "end": v(3.26, -0.07) * mm});
            skLineSegment(sketch, "E344", {"start": v(3.26, -0.07) * mm, "end": v(3.26, -0.07) * mm});
            skLineSegment(sketch, "E345", {"start": v(3.26, -0.07) * mm, "end": v(3.25, -0.07) * mm});
            skLineSegment(sketch, "E346", {"start": v(3.25, -0.07) * mm, "end": v(3.25, -0.07) * mm});
            skLineSegment(sketch, "E347", {"start": v(3.25, -0.07) * mm, "end": v(3.25, -0.06) * mm});
            skLineSegment(sketch, "E348", {"start": v(3.25, -0.06) * mm, "end": v(3.24, -0.06) * mm});
            skLineSegment(sketch, "E349", {"start": v(3.24, -0.06) * mm, "end": v(3.24, -0.06) * mm});
            skLineSegment(sketch, "E350", {"start": v(3.24, -0.06) * mm, "end": v(3.23, -0.06) * mm});
            skLineSegment(sketch, "E351", {"start": v(3.23, -0.06) * mm, "end": v(3.23, -0.06) * mm});
            skLineSegment(sketch, "E352", {"start": v(3.23, -0.06) * mm, "end": v(3.22, -0.05) * mm});
            skLineSegment(sketch, "E353", {"start": v(3.22, -0.05) * mm, "end": v(3.22, -0.05) * mm});
            skLineSegment(sketch, "E354", {"start": v(3.22, -0.05) * mm, "end": v(3.21, -0.05) * mm});
            skLineSegment(sketch, "E355", {"start": v(3.21, -0.05) * mm, "end": v(3.2, -0.05) * mm});
            skLineSegment(sketch, "E356", {"start": v(3.2, -0.05) * mm, "end": v(3.2, -0.04) * mm});
            skLineSegment(sketch, "E357", {"start": v(3.2, -0.04) * mm, "end": v(3.2, -0.04) * mm});
            skLineSegment(sketch, "E358", {"start": v(3.2, -0.04) * mm, "end": v(3.19, -0.04) * mm});
            skLineSegment(sketch, "E359", {"start": v(3.19, -0.04) * mm, "end": v(3.18, -0.03) * mm});
            skLineSegment(sketch, "E360", {"start": v(3.18, -0.03) * mm, "end": v(3.18, -0.03) * mm});
            skLineSegment(sketch, "E361", {"start": v(3.18, -0.03) * mm, "end": v(3.17, -0.03) * mm});
            skLineSegment(sketch, "E362", {"start": v(3.17, -0.03) * mm, "end": v(3.17, -0.03) * mm});
            skLineSegment(sketch, "E363", {"start": v(3.17, -0.03) * mm, "end": v(3.16, -0.03) * mm});
            skLineSegment(sketch, "E364", {"start": v(3.16, -0.03) * mm, "end": v(3.16, -0.02) * mm});
            skLineSegment(sketch, "E365", {"start": v(3.16, -0.02) * mm, "end": v(3.16, -0.02) * mm});
            skLineSegment(sketch, "E366", {"start": v(3.16, -0.02) * mm, "end": v(3.15, -0.02) * mm});
            skLineSegment(sketch, "E367", {"start": v(3.15, -0.02) * mm, "end": v(3.15, -0.02) * mm});
            skLineSegment(sketch, "E368", {"start": v(3.15, -0.02) * mm, "end": v(3.14, -0.02) * mm});
            skLineSegment(sketch, "E369", {"start": v(3.14, -0.02) * mm, "end": v(3.14, -0.01) * mm});
            skLineSegment(sketch, "E370", {"start": v(3.14, -0.01) * mm, "end": v(3.13, -0.01) * mm});
            skLineSegment(sketch, "E371", {"start": v(3.13, -0.01) * mm, "end": v(3.13, -0.01) * mm});
            skLineSegment(sketch, "E372", {"start": v(3.13, -0.01) * mm, "end": v(3.12, 0) * mm});
            skLineSegment(sketch, "E373", {"start": v(3.12, 0) * mm, "end": v(3.12, 0) * mm});
            skLineSegment(sketch, "E374", {"start": v(3.12, 0) * mm, "end": v(3.11, 0) * mm});
            skLineSegment(sketch, "E375", {"start": v(3.11, 0) * mm, "end": v(3.1, 0) * mm});
            skLineSegment(sketch, "E376", {"start": v(3.1, 0) * mm, "end": v(3.1, 0) * mm});
            skLineSegment(sketch, "E377", {"start": v(3.1, 0) * mm, "end": v(3.09, 0) * mm});
            skLineSegment(sketch, "E378", {"start": v(3.09, 0) * mm, "end": v(3.08, 0) * mm});
            skLineSegment(sketch, "E379", {"start": v(3.08, 0) * mm, "end": v(3.08, 0) * mm});
            skLineSegment(sketch, "E380", {"start": v(3.08, 0) * mm, "end": v(3.07, 0) * mm});
            skLineSegment(sketch, "E381", {"start": v(3.07, 0) * mm, "end": v(3.07, 0.01) * mm});
            skLineSegment(sketch, "E382", {"start": v(3.07, 0.01) * mm, "end": v(3.07, 0.01) * mm});
            skLineSegment(sketch, "E383", {"start": v(3.07, 0.01) * mm, "end": v(3.06, 0.01) * mm});
            skLineSegment(sketch, "E384", {"start": v(3.06, 0.01) * mm, "end": v(3.06, 0.01) * mm});
            skLineSegment(sketch, "E385", {"start": v(3.06, 0.01) * mm, "end": v(3.05, 0.02) * mm});
            skLineSegment(sketch, "E386", {"start": v(3.05, 0.02) * mm, "end": v(3.05, 0.02) * mm});
            skLineSegment(sketch, "E387", {"start": v(3.05, 0.02) * mm, "end": v(3.04, 0.02) * mm});
            skLineSegment(sketch, "E388", {"start": v(3.04, 0.02) * mm, "end": v(3.04, 0.02) * mm});
            skLineSegment(sketch, "E389", {"start": v(3.04, 0.02) * mm, "end": v(3.03, 0.02) * mm});
            skLineSegment(sketch, "E390", {"start": v(3.03, 0.02) * mm, "end": v(3.03, 0.02) * mm});
            skLineSegment(sketch, "E391", {"start": v(3.03, 0.02) * mm, "end": v(3.02, 0.03) * mm});
            skLineSegment(sketch, "E392", {"start": v(3.02, 0.03) * mm, "end": v(3.02, 0.03) * mm});
            skLineSegment(sketch, "E393", {"start": v(3.02, 0.03) * mm, "end": v(3.01, 0.03) * mm});
            skLineSegment(sketch, "E394", {"start": v(3.01, 0.03) * mm, "end": v(3, 0.03) * mm});
            skLineSegment(sketch, "E395", {"start": v(3, 0.03) * mm, "end": v(3, 0.03) * mm});
            skLineSegment(sketch, "E396", {"start": v(3, 0.03) * mm, "end": v(2.99, 0.03) * mm});
            skLineSegment(sketch, "E397", {"start": v(2.99, 0.03) * mm, "end": v(2.98, 0.03) * mm});
            skLineSegment(sketch, "E398", {"start": v(2.98, 0.03) * mm, "end": v(2.98, 0.03) * mm});
            skLineSegment(sketch, "E399", {"start": v(2.98, 0.03) * mm, "end": v(2.98, 0.04) * mm});
            skLineSegment(sketch, "E400", {"start": v(2.98, 0.04) * mm, "end": v(2.97, 0.04) * mm});
            skLineSegment(sketch, "E401", {"start": v(2.97, 0.04) * mm, "end": v(2.97, 0.04) * mm});
            skLineSegment(sketch, "E402", {"start": v(2.97, 0.04) * mm, "end": v(2.96, 0.04) * mm});
            skLineSegment(sketch, "E403", {"start": v(2.96, 0.04) * mm, "end": v(2.96, 0.04) * mm});
            skLineSegment(sketch, "E404", {"start": v(2.96, 0.04) * mm, "end": v(2.95, 0.04) * mm});
            skLineSegment(sketch, "E405", {"start": v(2.95, 0.04) * mm, "end": v(2.95, 0.04) * mm});
            skLineSegment(sketch, "E406", {"start": v(2.95, 0.04) * mm, "end": v(2.94, 0.04) * mm});
            skLineSegment(sketch, "E407", {"start": v(2.94, 0.04) * mm, "end": v(2.94, 0.04) * mm});
            skLineSegment(sketch, "E408", {"start": v(2.94, 0.04) * mm, "end": v(2.93, 0.04) * mm});
            skLineSegment(sketch, "E409", {"start": v(2.93, 0.04) * mm, "end": v(2.93, 0.04) * mm});
            skLineSegment(sketch, "E410", {"start": v(2.93, 0.04) * mm, "end": v(2.92, 0.04) * mm});
            skLineSegment(sketch, "E411", {"start": v(2.92, 0.04) * mm, "end": v(2.92, 0.04) * mm});
            skLineSegment(sketch, "E412", {"start": v(2.92, 0.04) * mm, "end": v(2.91, 0.04) * mm});
            skLineSegment(sketch, "E413", {"start": v(2.91, 0.04) * mm, "end": v(2.9, 0.05) * mm});
            skLineSegment(sketch, "E414", {"start": v(2.9, 0.05) * mm, "end": v(2.9, 0.05) * mm});
            skLineSegment(sketch, "E415", {"start": v(2.9, 0.05) * mm, "end": v(2.89, 0.05) * mm});
            skLineSegment(sketch, "E416", {"start": v(2.89, 0.05) * mm, "end": v(2.88, 0.05) * mm});
            skLineSegment(sketch, "E417", {"start": v(2.88, 0.05) * mm, "end": v(2.88, 0.05) * mm});
            skLineSegment(sketch, "E418", {"start": v(2.88, 0.05) * mm, "end": v(2.87, 0.06) * mm});
            skLineSegment(sketch, "E419", {"start": v(2.87, 0.06) * mm, "end": v(2.87, 0.06) * mm});
            skLineSegment(sketch, "E420", {"start": v(2.87, 0.06) * mm, "end": v(2.86, 0.06) * mm});
            skLineSegment(sketch, "E421", {"start": v(2.86, 0.06) * mm, "end": v(2.86, 0.07) * mm});
            skLineSegment(sketch, "E422", {"start": v(2.86, 0.07) * mm, "end": v(2.85, 0.07) * mm});
            skLineSegment(sketch, "E423", {"start": v(2.95, 6.23) * mm, "end": v(2.95, 6.3) * mm});
            skLineSegment(sketch, "E424", {"start": v(2.95, 6.3) * mm, "end": v(2.95, 6.37) * mm});
            skLineSegment(sketch, "E425", {"start": v(2.95, 6.37) * mm, "end": v(2.96, 6.38) * mm});
            skLineSegment(sketch, "E426", {"start": v(2.96, 6.38) * mm, "end": v(2.96, 6.38) * mm});
            skLineSegment(sketch, "E427", {"start": v(2.96, 6.38) * mm, "end": v(2.97, 6.39) * mm});
            skLineSegment(sketch, "E428", {"start": v(2.97, 6.39) * mm, "end": v(2.97, 6.39) * mm});
            skLineSegment(sketch, "E429", {"start": v(2.97, 6.39) * mm, "end": v(2.98, 6.4) * mm});
            skLineSegment(sketch, "E430", {"start": v(2.98, 6.4) * mm, "end": v(2.98, 6.4) * mm});
            skLineSegment(sketch, "E431", {"start": v(2.98, 6.4) * mm, "end": v(2.99, 6.4) * mm});
            skLineSegment(sketch, "E432", {"start": v(2.99, 6.4) * mm, "end": v(3, 6.4) * mm});
            skLineSegment(sketch, "E433", {"start": v(3, 6.4) * mm, "end": v(3, 6.4) * mm});
            skLineSegment(sketch, "E434", {"start": v(3, 6.4) * mm, "end": v(3.01, 6.4) * mm});
            skLineSegment(sketch, "E435", {"start": v(3.01, 6.4) * mm, "end": v(3.02, 6.4) * mm});
            skLineSegment(sketch, "E436", {"start": v(3.02, 6.4) * mm, "end": v(3.02, 6.4) * mm});
            skLineSegment(sketch, "E437", {"start": v(3.02, 6.4) * mm, "end": v(3.03, 6.4) * mm});
            skLineSegment(sketch, "E438", {"start": v(3.03, 6.4) * mm, "end": v(3.03, 6.4) * mm});
            skLineSegment(sketch, "E439", {"start": v(3.03, 6.4) * mm, "end": v(3.04, 6.4) * mm});
            skLineSegment(sketch, "E440", {"start": v(3.04, 6.4) * mm, "end": v(3.04, 6.4) * mm});
            skLineSegment(sketch, "E441", {"start": v(3.04, 6.4) * mm, "end": v(3.05, 6.4) * mm});
            skLineSegment(sketch, "E442", {"start": v(3.05, 6.4) * mm, "end": v(3.05, 6.4) * mm});
            skLineSegment(sketch, "E443", {"start": v(3.05, 6.4) * mm, "end": v(3.06, 6.41) * mm});
            skLineSegment(sketch, "E444", {"start": v(3.06, 6.41) * mm, "end": v(3.06, 6.41) * mm});
            skLineSegment(sketch, "E445", {"start": v(3.06, 6.41) * mm, "end": v(3.07, 6.41) * mm});
            skLineSegment(sketch, "E446", {"start": v(3.07, 6.41) * mm, "end": v(3.07, 6.42) * mm});
            skLineSegment(sketch, "E447", {"start": v(3.07, 6.42) * mm, "end": v(3.08, 6.42) * mm});
            skLineSegment(sketch, "E448", {"start": v(3.08, 6.42) * mm, "end": v(3.08, 6.42) * mm});
            skLineSegment(sketch, "E449", {"start": v(3.08, 6.42) * mm, "end": v(3.09, 6.42) * mm});
            skLineSegment(sketch, "E450", {"start": v(3.09, 6.42) * mm, "end": v(3.1, 6.42) * mm});
            skLineSegment(sketch, "E451", {"start": v(3.1, 6.42) * mm, "end": v(3.1, 6.42) * mm});
            skLineSegment(sketch, "E452", {"start": v(3.1, 6.42) * mm, "end": v(3.1, 6.43) * mm});
            skLineSegment(sketch, "E453", {"start": v(3.1, 6.43) * mm, "end": v(3.11, 6.43) * mm});
            skLineSegment(sketch, "E454", {"start": v(3.11, 6.43) * mm, "end": v(3.12, 6.43) * mm});
            skLineSegment(sketch, "E455", {"start": v(3.12, 6.43) * mm, "end": v(3.12, 6.43) * mm});
            skLineSegment(sketch, "E456", {"start": v(3.12, 6.43) * mm, "end": v(3.13, 6.43) * mm});
            skLineSegment(sketch, "E457", {"start": v(3.13, 6.43) * mm, "end": v(3.13, 6.43) * mm});
            skLineSegment(sketch, "E458", {"start": v(3.13, 6.43) * mm, "end": v(3.14, 6.43) * mm});
            skLineSegment(sketch, "E459", {"start": v(3.14, 6.43) * mm, "end": v(3.14, 6.44) * mm});
            skLineSegment(sketch, "E460", {"start": v(3.14, 6.44) * mm, "end": v(3.15, 6.44) * mm});
            skLineSegment(sketch, "E461", {"start": v(3.15, 6.44) * mm, "end": v(3.15, 6.44) * mm});
            skLineSegment(sketch, "E462", {"start": v(3.15, 6.44) * mm, "end": v(3.16, 6.44) * mm});
            skLineSegment(sketch, "E463", {"start": v(3.16, 6.44) * mm, "end": v(3.16, 6.44) * mm});
            skLineSegment(sketch, "E464", {"start": v(3.16, 6.44) * mm, "end": v(3.17, 6.45) * mm});
            skLineSegment(sketch, "E465", {"start": v(3.17, 6.45) * mm, "end": v(3.17, 6.45) * mm});
            skLineSegment(sketch, "E466", {"start": v(3.17, 6.45) * mm, "end": v(3.18, 6.45) * mm});
            skLineSegment(sketch, "E467", {"start": v(3.18, 6.45) * mm, "end": v(3.18, 6.45) * mm});
            skLineSegment(sketch, "E468", {"start": v(3.18, 6.45) * mm, "end": v(3.19, 6.45) * mm});
            skLineSegment(sketch, "E469", {"start": v(3.19, 6.45) * mm, "end": v(3.2, 6.46) * mm});
            skLineSegment(sketch, "E470", {"start": v(3.2, 6.46) * mm, "end": v(3.2, 6.46) * mm});
            skLineSegment(sketch, "E471", {"start": v(3.2, 6.46) * mm, "end": v(3.21, 6.46) * mm});
            skLineSegment(sketch, "E472", {"start": v(3.21, 6.46) * mm, "end": v(3.22, 6.47) * mm});
            skLineSegment(sketch, "E473", {"start": v(3.22, 6.47) * mm, "end": v(3.22, 6.47) * mm});
            skLineSegment(sketch, "E474", {"start": v(3.22, 6.47) * mm, "end": v(3.23, 6.47) * mm});
            skLineSegment(sketch, "E475", {"start": v(3.23, 6.47) * mm, "end": v(3.23, 6.47) * mm});
            skLineSegment(sketch, "E476", {"start": v(3.23, 6.47) * mm, "end": v(3.24, 6.48) * mm});
            skLineSegment(sketch, "E477", {"start": v(3.24, 6.48) * mm, "end": v(3.24, 6.48) * mm});
            skLineSegment(sketch, "E478", {"start": v(3.24, 6.48) * mm, "end": v(3.25, 6.48) * mm});
            skLineSegment(sketch, "E479", {"start": v(3.25, 6.48) * mm, "end": v(3.25, 6.48) * mm});
            skLineSegment(sketch, "E480", {"start": v(3.25, 6.48) * mm, "end": v(3.26, 6.48) * mm});
            skLineSegment(sketch, "E481", {"start": v(3.26, 6.48) * mm, "end": v(3.26, 6.49) * mm});
            skLineSegment(sketch, "E482", {"start": v(3.26, 6.49) * mm, "end": v(3.26, 6.49) * mm});
            skLineSegment(sketch, "E483", {"start": v(3.26, 6.49) * mm, "end": v(3.27, 6.5) * mm});
            skLineSegment(sketch, "E484", {"start": v(3.27, 6.5) * mm, "end": v(3.27, 6.5) * mm});
            skLineSegment(sketch, "E485", {"start": v(3.27, 6.5) * mm, "end": v(3.28, 6.5) * mm});
            skLineSegment(sketch, "E486", {"start": v(3.28, 6.5) * mm, "end": v(3.28, 6.5) * mm});
            skLineSegment(sketch, "E487", {"start": v(3.28, 6.5) * mm, "end": v(3.29, 6.5) * mm});
            skLineSegment(sketch, "E488", {"start": v(3.29, 6.5) * mm, "end": v(3.3, 6.5) * mm});
            skLineSegment(sketch, "E489", {"start": v(3.3, 6.5) * mm, "end": v(3.3, 6.5) * mm});
            skLineSegment(sketch, "E490", {"start": v(3.3, 6.5) * mm, "end": v(3.3, 6.51) * mm});
            skLineSegment(sketch, "E491", {"start": v(3.3, 6.51) * mm, "end": v(3.31, 6.51) * mm});
            skLineSegment(sketch, "E492", {"start": v(3.31, 6.51) * mm, "end": v(3.32, 6.52) * mm});
            skLineSegment(sketch, "E493", {"start": v(3.32, 6.52) * mm, "end": v(3.32, 6.52) * mm});
            skLineSegment(sketch, "E494", {"start": v(3.32, 6.52) * mm, "end": v(3.33, 6.52) * mm});
            skLineSegment(sketch, "E495", {"start": v(3.33, 6.52) * mm, "end": v(3.33, 6.52) * mm});
            skLineSegment(sketch, "E496", {"start": v(3.33, 6.52) * mm, "end": v(3.33, 6.53) * mm});
            skLineSegment(sketch, "E497", {"start": v(3.33, 6.53) * mm, "end": v(3.34, 6.53) * mm});
            skLineSegment(sketch, "E498", {"start": v(3.34, 6.53) * mm, "end": v(3.34, 6.53) * mm});
            skLineSegment(sketch, "E499", {"start": v(3.34, 6.53) * mm, "end": v(3.35, 6.53) * mm});
            skLineSegment(sketch, "E500", {"start": v(3.35, 6.53) * mm, "end": v(3.35, 6.54) * mm});
            skLineSegment(sketch, "E501", {"start": v(3.35, 6.54) * mm, "end": v(3.36, 6.54) * mm});
            skLineSegment(sketch, "E502", {"start": v(3.36, 6.54) * mm, "end": v(3.36, 6.54) * mm});
            skLineSegment(sketch, "E503", {"start": v(3.36, 6.54) * mm, "end": v(3.37, 6.55) * mm});
            skLineSegment(sketch, "E504", {"start": v(3.37, 6.55) * mm, "end": v(3.37, 6.55) * mm});
            skLineSegment(sketch, "E505", {"start": v(3.37, 6.55) * mm, "end": v(3.38, 6.55) * mm});
            skLineSegment(sketch, "E506", {"start": v(3.38, 6.55) * mm, "end": v(3.38, 6.55) * mm});
            skLineSegment(sketch, "E507", {"start": v(3.38, 6.55) * mm, "end": v(3.39, 6.56) * mm});
            skLineSegment(sketch, "E508", {"start": v(3.39, 6.56) * mm, "end": v(3.4, 6.56) * mm});
            skLineSegment(sketch, "E509", {"start": v(3.4, 6.56) * mm, "end": v(3.38, 6.7) * mm});
            skLineSegment(sketch, "E510", {"start": v(3.38, 6.7) * mm, "end": v(3.37, 6.7) * mm});
            skLineSegment(sketch, "E511", {"start": v(3.37, 6.7) * mm, "end": v(3.37, 6.71) * mm});
            skLineSegment(sketch, "E512", {"start": v(3.37, 6.71) * mm, "end": v(3.36, 6.71) * mm});
            skLineSegment(sketch, "E513", {"start": v(3.36, 6.71) * mm, "end": v(3.36, 6.71) * mm});
            skLineSegment(sketch, "E514", {"start": v(3.36, 6.71) * mm, "end": v(3.35, 6.72) * mm});
            skLineSegment(sketch, "E515", {"start": v(3.35, 6.72) * mm, "end": v(3.35, 6.72) * mm});
            skLineSegment(sketch, "E516", {"start": v(3.35, 6.72) * mm, "end": v(3.34, 6.72) * mm});
            skLineSegment(sketch, "E517", {"start": v(3.34, 6.72) * mm, "end": v(3.34, 6.72) * mm});
            skLineSegment(sketch, "E518", {"start": v(3.34, 6.72) * mm, "end": v(3.33, 6.72) * mm});
            skLineSegment(sketch, "E519", {"start": v(3.33, 6.72) * mm, "end": v(3.33, 6.72) * mm});
            skLineSegment(sketch, "E520", {"start": v(3.33, 6.72) * mm, "end": v(3.32, 6.73) * mm});
            skLineSegment(sketch, "E521", {"start": v(3.32, 6.73) * mm, "end": v(3.32, 6.73) * mm});
            skLineSegment(sketch, "E522", {"start": v(3.32, 6.73) * mm, "end": v(3.31, 6.73) * mm});
            skLineSegment(sketch, "E523", {"start": v(3.31, 6.73) * mm, "end": v(3.3, 6.73) * mm});
            skLineSegment(sketch, "E524", {"start": v(3.3, 6.73) * mm, "end": v(3.3, 6.73) * mm});
            skLineSegment(sketch, "E525", {"start": v(3.3, 6.73) * mm, "end": v(3.3, 6.74) * mm});
            skLineSegment(sketch, "E526", {"start": v(3.3, 6.74) * mm, "end": v(3.3, 6.74) * mm});
            skLineSegment(sketch, "E527", {"start": v(3.3, 6.74) * mm, "end": v(3.29, 6.74) * mm});
            skLineSegment(sketch, "E528", {"start": v(3.29, 6.74) * mm, "end": v(3.28, 6.74) * mm});
            skLineSegment(sketch, "E529", {"start": v(3.28, 6.74) * mm, "end": v(3.28, 6.74) * mm});
            skLineSegment(sketch, "E530", {"start": v(3.28, 6.74) * mm, "end": v(3.27, 6.74) * mm});
            skLineSegment(sketch, "E531", {"start": v(3.27, 6.74) * mm, "end": v(3.27, 6.74) * mm});
            skLineSegment(sketch, "E532", {"start": v(3.27, 6.74) * mm, "end": v(3.26, 6.75) * mm});
            skLineSegment(sketch, "E533", {"start": v(3.26, 6.75) * mm, "end": v(3.26, 6.75) * mm});
            skLineSegment(sketch, "E534", {"start": v(3.26, 6.75) * mm, "end": v(3.25, 6.75) * mm});
            skLineSegment(sketch, "E535", {"start": v(3.25, 6.75) * mm, "end": v(3.25, 6.75) * mm});
            skLineSegment(sketch, "E536", {"start": v(3.25, 6.75) * mm, "end": v(3.24, 6.75) * mm});
            skLineSegment(sketch, "E537", {"start": v(3.24, 6.75) * mm, "end": v(3.24, 6.75) * mm});
            skLineSegment(sketch, "E538", {"start": v(3.24, 6.75) * mm, "end": v(3.23, 6.75) * mm});
            skLineSegment(sketch, "E539", {"start": v(3.23, 6.75) * mm, "end": v(3.23, 6.75) * mm});
            skLineSegment(sketch, "E540", {"start": v(3.23, 6.75) * mm, "end": v(3.22, 6.76) * mm});
            skLineSegment(sketch, "E541", {"start": v(3.22, 6.76) * mm, "end": v(3.22, 6.76) * mm});
            skLineSegment(sketch, "E542", {"start": v(3.22, 6.76) * mm, "end": v(3.21, 6.76) * mm});
            skLineSegment(sketch, "E543", {"start": v(3.21, 6.76) * mm, "end": v(3.2, 6.76) * mm});
            skLineSegment(sketch, "E544", {"start": v(3.2, 6.76) * mm, "end": v(3.2, 6.76) * mm});
            skLineSegment(sketch, "E545", {"start": v(3.2, 6.76) * mm, "end": v(3.19, 6.77) * mm});
            skLineSegment(sketch, "E546", {"start": v(3.19, 6.77) * mm, "end": v(3.18, 6.77) * mm});
            skLineSegment(sketch, "E547", {"start": v(3.18, 6.77) * mm, "end": v(3.18, 6.77) * mm});
            skLineSegment(sketch, "E548", {"start": v(3.18, 6.77) * mm, "end": v(3.17, 6.77) * mm});
            skLineSegment(sketch, "E549", {"start": v(3.17, 6.77) * mm, "end": v(3.17, 6.77) * mm});
            skLineSegment(sketch, "E550", {"start": v(3.17, 6.77) * mm, "end": v(3.16, 6.77) * mm});
            skLineSegment(sketch, "E551", {"start": v(3.16, 6.77) * mm, "end": v(3.16, 6.77) * mm});
            skLineSegment(sketch, "E552", {"start": v(3.16, 6.77) * mm, "end": v(3.15, 6.77) * mm});
            skLineSegment(sketch, "E553", {"start": v(3.15, 6.77) * mm, "end": v(3.15, 6.77) * mm});
            skLineSegment(sketch, "E554", {"start": v(3.15, 6.77) * mm, "end": v(3.14, 6.77) * mm});
            skLineSegment(sketch, "E555", {"start": v(3.14, 6.77) * mm, "end": v(3.14, 6.77) * mm});
            skLineSegment(sketch, "E556", {"start": v(3.14, 6.77) * mm, "end": v(3.13, 6.78) * mm});
            skLineSegment(sketch, "E557", {"start": v(3.13, 6.78) * mm, "end": v(3.13, 6.78) * mm});
            skLineSegment(sketch, "E558", {"start": v(3.13, 6.78) * mm, "end": v(3.12, 6.78) * mm});
            skLineSegment(sketch, "E559", {"start": v(3.12, 6.78) * mm, "end": v(3.12, 6.78) * mm});
            skLineSegment(sketch, "E560", {"start": v(3.12, 6.78) * mm, "end": v(3.11, 6.78) * mm});
            skLineSegment(sketch, "E561", {"start": v(3.11, 6.78) * mm, "end": v(3.1, 6.78) * mm});
            skLineSegment(sketch, "E562", {"start": v(3.1, 6.78) * mm, "end": v(3.1, 6.78) * mm});
            skLineSegment(sketch, "E563", {"start": v(3.1, 6.78) * mm, "end": v(3.09, 6.78) * mm});
            skLineSegment(sketch, "E564", {"start": v(3.09, 6.78) * mm, "end": v(3.08, 6.78) * mm});
            skLineSegment(sketch, "E565", {"start": v(3.08, 6.78) * mm, "end": v(3.08, 6.78) * mm});
            skLineSegment(sketch, "E566", {"start": v(3.08, 6.78) * mm, "end": v(3.07, 6.78) * mm});
            skLineSegment(sketch, "E567", {"start": v(3.07, 6.78) * mm, "end": v(3.07, 6.78) * mm});
            skLineSegment(sketch, "E568", {"start": v(3.07, 6.78) * mm, "end": v(3.06, 6.78) * mm});
            skLineSegment(sketch, "E569", {"start": v(3.06, 6.78) * mm, "end": v(3.06, 6.79) * mm});
            skLineSegment(sketch, "E570", {"start": v(3.06, 6.79) * mm, "end": v(3.06, 6.79) * mm});
            skLineSegment(sketch, "E571", {"start": v(3.06, 6.79) * mm, "end": v(3.05, 6.79) * mm});
            skLineSegment(sketch, "E572", {"start": v(3.05, 6.79) * mm, "end": v(3.05, 6.79) * mm});
            skLineSegment(sketch, "E573", {"start": v(3.05, 6.79) * mm, "end": v(3.04, 6.79) * mm});
            skLineSegment(sketch, "E574", {"start": v(3.04, 6.79) * mm, "end": v(3.04, 6.79) * mm});
            skLineSegment(sketch, "E575", {"start": v(3.04, 6.79) * mm, "end": v(3.03, 6.79) * mm});
            skLineSegment(sketch, "E576", {"start": v(3.03, 6.79) * mm, "end": v(3.03, 6.79) * mm});
            skLineSegment(sketch, "E577", {"start": v(3.03, 6.79) * mm, "end": v(3.02, 6.79) * mm});
            skLineSegment(sketch, "E578", {"start": v(3.02, 6.79) * mm, "end": v(3.02, 6.79) * mm});
            skLineSegment(sketch, "E579", {"start": v(3.02, 6.79) * mm, "end": v(3.01, 6.79) * mm});
            skLineSegment(sketch, "E580", {"start": v(3.01, 6.79) * mm, "end": v(3, 6.79) * mm});
            skLineSegment(sketch, "E581", {"start": v(3, 6.79) * mm, "end": v(3, 6.79) * mm});
            skLineSegment(sketch, "E582", {"start": v(3, 6.79) * mm, "end": v(2.99, 6.79) * mm});
            skLineSegment(sketch, "E583", {"start": v(2.99, 6.79) * mm, "end": v(2.98, 6.79) * mm});
            skLineSegment(sketch, "E584", {"start": v(2.98, 6.79) * mm, "end": v(2.98, 6.79) * mm});
            skLineSegment(sketch, "E585", {"start": v(2.98, 6.79) * mm, "end": v(2.97, 6.79) * mm});
            skLineSegment(sketch, "E586", {"start": v(2.97, 6.79) * mm, "end": v(2.97, 6.79) * mm});
            skLineSegment(sketch, "E587", {"start": v(2.97, 6.79) * mm, "end": v(2.96, 6.79) * mm});
            skLineSegment(sketch, "E588", {"start": v(2.96, 6.79) * mm, "end": v(2.96, 6.79) * mm});
            skLineSegment(sketch, "E589", {"start": v(2.96, 6.79) * mm, "end": v(2.95, 6.79) * mm});
            skLineSegment(sketch, "E590", {"start": v(2.95, 6.79) * mm, "end": v(2.95, 6.79) * mm});
            skLineSegment(sketch, "E591", {"start": v(2.95, 6.79) * mm, "end": v(2.94, 6.8) * mm});
            skLineSegment(sketch, "E592", {"start": v(2.94, 6.8) * mm, "end": v(2.94, 6.8) * mm});
            skLineSegment(sketch, "E593", {"start": v(2.94, 6.8) * mm, "end": v(2.93, 6.8) * mm});
            skLineSegment(sketch, "E594", {"start": v(2.93, 6.8) * mm, "end": v(2.93, 6.8) * mm});
            skLineSegment(sketch, "E595", {"start": v(2.93, 6.8) * mm, "end": v(2.92, 6.8) * mm});
            skLineSegment(sketch, "E596", {"start": v(2.92, 6.8) * mm, "end": v(2.92, 6.8) * mm});
            skLineSegment(sketch, "E597", {"start": v(2.92, 6.8) * mm, "end": v(2.91, 6.8) * mm});
            skLineSegment(sketch, "E598", {"start": v(-0.45, 10.34) * mm, "end": v(0.3, 10.35) * mm});
            skLineSegment(sketch, "E599", {"start": v(0, 0) * mm, "end": v(-0.4, 10.34) * mm});
            skLineSegment(sketch, "E600", {"start": v(0, 0) * mm, "end": v(0.28, 10.35) * mm});
            skLineSegment(sketch, "E601", {"start": v(0, 6.3) * mm, "end": v(2.91, 6.8) * mm});
            skLineSegment(sketch, "E602", {"start": v(0, 6.3) * mm, "end": v(2.95, 6.23) * mm});
            skSolve(sketch);
        }
        {
            var Q0;
            {var subQ3=sQuery(id+"F0.wireOp",EDGE,"E6");Q0=makeQuery(id+"F0.imprint","IMPRINT",FACE,{"disambiguationData":[TD([[makeQuery(id+"F0.imprint","IMPRINT",EDGE,{"derivedFrom":subQ3}),-1.0]])]});}
            var Q1;
            Q1=makeQuery(id+"F0.imprint","IMPRINT",FACE,{"disambiguationData":[TD([[makeQuery(id+"F0.imprint","IMPRINT",EDGE,{"derivedFrom":sQuery(id+"F0.wireOp",EDGE,"E1")}),-1.0]])]});
            extrude(context, id + "F1", {"entities" : qUnion([Q0, Q1]), "depth" : 5 * mm});
        }
        {
            var Q0;
            Q0=makeQuery(id+"F1.opExtrude","SWEPT_BODY",BODY,{"disambiguationData":[OSD([sQuery(id+"F0.wireOp",EDGE,"E6"),sQuery(id+"F0.wireOp",EDGE,"E7"),sQuery(id+"F0.wireOp",EDGE,"E8"),sQuery(id+"F0.wireOp",EDGE,"E9"),sQuery(id+"F0.wireOp",EDGE,"E10"),sQuery(id+"F0.wireOp",EDGE,"E11"),sQuery(id+"F0.wireOp",EDGE,"E11"),sQuery(id+"F0.wireOp",EDGE,"E12"),sQuery(id+"F0.wireOp",EDGE,"E13"),sQuery(id+"F0.wireOp",EDGE,"E14"),sQuery(id+"F0.wireOp",EDGE,"E14"),sQuery(id+"F0.wireOp",EDGE,"E14"),sQuery(id+"F0.wireOp",EDGE,"E15"),sQuery(id+"F0.wireOp",EDGE,"E16"),sQuery(id+"F0.wireOp",EDGE,"E17"),sQuery(id+"F0.wireOp",EDGE,"E17"),sQuery(id+"F0.wireOp",EDGE,"E18"),sQuery(id+"F0.wireOp",EDGE,"E19"),sQuery(id+"F0.wireOp",EDGE,"E20"),sQuery(id+"F0.wireOp",EDGE,"E21"),sQuery(id+"F0.wireOp",EDGE,"E22"),sQuery(id+"F0.wireOp",EDGE,"E23"),sQuery(id+"F0.wireOp",EDGE,"E24"),sQuery(id+"F0.wireOp",EDGE,"E25"),sQuery(id+"F0.wireOp",EDGE,"E26"),sQuery(id+"F0.wireOp",EDGE,"E27"),sQuery(id+"F0.wireOp",EDGE,"E28"),sQuery(id+"F0.wireOp",EDGE,"E29"),sQuery(id+"F0.wireOp",EDGE,"E30"),sQuery(id+"F0.wireOp",EDGE,"E31"),sQuery(id+"F0.wireOp",EDGE,"E32"),sQuery(id+"F0.wireOp",EDGE,"E33"),sQuery(id+"F0.wireOp",EDGE,"E33"),sQuery(id+"F0.wireOp",EDGE,"E33"),sQuery(id+"F0.wireOp",EDGE,"E33"),sQuery(id+"F0.wireOp",EDGE,"E34"),sQuery(id+"F0.wireOp",EDGE,"E35"),sQuery(id+"F0.wireOp",EDGE,"E36"),sQuery(id+"F0.wireOp",EDGE,"E37"),sQuery(id+"F0.wireOp",EDGE,"E38"),sQuery(id+"F0.wireOp",EDGE,"E39"),sQuery(id+"F0.wireOp",EDGE,"E40"),sQuery(id+"F0.wireOp",EDGE,"E41"),sQuery(id+"F0.wireOp",EDGE,"E42"),sQuery(id+"F0.wireOp",EDGE,"E42"),sQuery(id+"F0.wireOp",EDGE,"E43"),sQuery(id+"F0.wireOp",EDGE,"E44"),sQuery(id+"F0.wireOp",EDGE,"E45"),sQuery(id+"F0.wireOp",EDGE,"E46"),sQuery(id+"F0.wireOp",EDGE,"E47"),sQuery(id+"F0.wireOp",EDGE,"E48"),sQuery(id+"F0.wireOp",EDGE,"E49"),sQuery(id+"F0.wireOp",EDGE,"E50"),sQuery(id+"F0.wireOp",EDGE,"E51"),sQuery(id+"F0.wireOp",EDGE,"E52"),sQuery(id+"F0.wireOp",EDGE,"E52"),sQuery(id+"F0.wireOp",EDGE,"E53"),sQuery(id+"F0.wireOp",EDGE,"E54"),sQuery(id+"F0.wireOp",EDGE,"E55"),sQuery(id+"F0.wireOp",EDGE,"E56"),sQuery(id+"F0.wireOp",EDGE,"E57"),sQuery(id+"F0.wireOp",EDGE,"E58"),sQuery(id+"F0.wireOp",EDGE,"E59"),sQuery(id+"F0.wireOp",EDGE,"E60"),sQuery(id+"F0.wireOp",EDGE,"E61"),sQuery(id+"F0.wireOp",EDGE,"E62"),sQuery(id+"F0.wireOp",EDGE,"E63"),sQuery(id+"F0.wireOp",EDGE,"E64"),sQuery(id+"F0.wireOp",EDGE,"E65"),sQuery(id+"F0.wireOp",EDGE,"E66"),sQuery(id+"F0.wireOp",EDGE,"E67"),sQuery(id+"F0.wireOp",EDGE,"E67"),sQuery(id+"F0.wireOp",EDGE,"E68"),sQuery(id+"F0.wireOp",EDGE,"E69"),sQuery(id+"F0.wireOp",EDGE,"E70"),sQuery(id+"F0.wireOp",EDGE,"E71"),sQuery(id+"F0.wireOp",EDGE,"E72"),sQuery(id+"F0.wireOp",EDGE,"E72"),sQuery(id+"F0.wireOp",EDGE,"E72"),sQuery(id+"F0.wireOp",EDGE,"E73"),sQuery(id+"F0.wireOp",EDGE,"E74"),sQuery(id+"F0.wireOp",EDGE,"E75"),sQuery(id+"F0.wireOp",EDGE,"E76"),sQuery(id+"F0.wireOp",EDGE,"E77"),sQuery(id+"F0.wireOp",EDGE,"E78"),sQuery(id+"F0.wireOp",EDGE,"E79"),sQuery(id+"F0.wireOp",EDGE,"E80"),sQuery(id+"F0.wireOp",EDGE,"E81"),sQuery(id+"F0.wireOp",EDGE,"E82"),sQuery(id+"F0.wireOp",EDGE,"E83"),sQuery(id+"F0.wireOp",EDGE,"E84"),sQuery(id+"F0.wireOp",EDGE,"E84"),sQuery(id+"F0.wireOp",EDGE,"E85"),sQuery(id+"F0.wireOp",EDGE,"E86"),sQuery(id+"F0.wireOp",EDGE,"E87"),sQuery(id+"F0.wireOp",EDGE,"E88"),sQuery(id+"F0.wireOp",EDGE,"E89"),sQuery(id+"F0.wireOp",EDGE,"E90"),sQuery(id+"F0.wireOp",EDGE,"E91"),sQuery(id+"F0.wireOp",EDGE,"E92"),sQuery(id+"F0.wireOp",EDGE,"E93"),sQuery(id+"F0.wireOp",EDGE,"E94"),sQuery(id+"F0.wireOp",EDGE,"E95"),sQuery(id+"F0.wireOp",EDGE,"E96"),sQuery(id+"F0.wireOp",EDGE,"E97"),sQuery(id+"F0.wireOp",EDGE,"E98"),sQuery(id+"F0.wireOp",EDGE,"E99"),sQuery(id+"F0.wireOp",EDGE,"E100"),sQuery(id+"F0.wireOp",EDGE,"E101"),sQuery(id+"F0.wireOp",EDGE,"E101"),sQuery(id+"F0.wireOp",EDGE,"E102"),sQuery(id+"F0.wireOp",EDGE,"E103"),sQuery(id+"F0.wireOp",EDGE,"E104"),sQuery(id+"F0.wireOp",EDGE,"E105"),sQuery(id+"F0.wireOp",EDGE,"E106"),sQuery(id+"F0.wireOp",EDGE,"E107"),sQuery(id+"F0.wireOp",EDGE,"E108"),sQuery(id+"F0.wireOp",EDGE,"E109"),sQuery(id+"F0.wireOp",EDGE,"E110"),sQuery(id+"F0.wireOp",EDGE,"E111"),sQuery(id+"F0.wireOp",EDGE,"E112"),sQuery(id+"F0.wireOp",EDGE,"E113"),sQuery(id+"F0.wireOp",EDGE,"E113"),sQuery(id+"F0.wireOp",EDGE,"E113"),sQuery(id+"F0.wireOp",EDGE,"E114"),sQuery(id+"F0.wireOp",EDGE,"E115"),sQuery(id+"F0.wireOp",EDGE,"E116"),sQuery(id+"F0.wireOp",EDGE,"E117"),sQuery(id+"F0.wireOp",EDGE,"E118"),sQuery(id+"F0.wireOp",EDGE,"E118"),sQuery(id+"F0.wireOp",EDGE,"E119"),sQuery(id+"F0.wireOp",EDGE,"E120"),sQuery(id+"F0.wireOp",EDGE,"E121"),sQuery(id+"F0.wireOp",EDGE,"E122"),sQuery(id+"F0.wireOp",EDGE,"E123"),sQuery(id+"F0.wireOp",EDGE,"E124"),sQuery(id+"F0.wireOp",EDGE,"E125"),sQuery(id+"F0.wireOp",EDGE,"E126"),sQuery(id+"F0.wireOp",EDGE,"E127"),sQuery(id+"F0.wireOp",EDGE,"E128"),sQuery(id+"F0.wireOp",EDGE,"E129"),sQuery(id+"F0.wireOp",EDGE,"E130"),sQuery(id+"F0.wireOp",EDGE,"E131"),sQuery(id+"F0.wireOp",EDGE,"E132"),sQuery(id+"F0.wireOp",EDGE,"E133"),sQuery(id+"F0.wireOp",EDGE,"E133"),sQuery(id+"F0.wireOp",EDGE,"E134"),sQuery(id+"F0.wireOp",EDGE,"E135"),sQuery(id+"F0.wireOp",EDGE,"E136"),sQuery(id+"F0.wireOp",EDGE,"E137"),sQuery(id+"F0.wireOp",EDGE,"E138"),sQuery(id+"F0.wireOp",EDGE,"E139"),sQuery(id+"F0.wireOp",EDGE,"E140"),sQuery(id+"F0.wireOp",EDGE,"E141"),sQuery(id+"F0.wireOp",EDGE,"E142"),sQuery(id+"F0.wireOp",EDGE,"E143"),sQuery(id+"F0.wireOp",EDGE,"E143"),sQuery(id+"F0.wireOp",EDGE,"E144"),sQuery(id+"F0.wireOp",EDGE,"E145"),sQuery(id+"F0.wireOp",EDGE,"E146"),sQuery(id+"F0.wireOp",EDGE,"E147"),sQuery(id+"F0.wireOp",EDGE,"E148"),sQuery(id+"F0.wireOp",EDGE,"E149"),sQuery(id+"F0.wireOp",EDGE,"E150"),sQuery(id+"F0.wireOp",EDGE,"E151"),sQuery(id+"F0.wireOp",EDGE,"E152"),sQuery(id+"F0.wireOp",EDGE,"E152"),sQuery(id+"F0.wireOp",EDGE,"E152"),sQuery(id+"F0.wireOp",EDGE,"E152"),sQuery(id+"F0.wireOp",EDGE,"E153"),sQuery(id+"F0.wireOp",EDGE,"E154"),sQuery(id+"F0.wireOp",EDGE,"E155"),sQuery(id+"F0.wireOp",EDGE,"E156"),sQuery(id+"F0.wireOp",EDGE,"E157"),sQuery(id+"F0.wireOp",EDGE,"E158"),sQuery(id+"F0.wireOp",EDGE,"E159"),sQuery(id+"F0.wireOp",EDGE,"E160"),sQuery(id+"F0.wireOp",EDGE,"E161"),sQuery(id+"F0.wireOp",EDGE,"E162"),sQuery(id+"F0.wireOp",EDGE,"E163"),sQuery(id+"F0.wireOp",EDGE,"E164"),sQuery(id+"F0.wireOp",EDGE,"E165"),sQuery(id+"F0.wireOp",EDGE,"E166"),sQuery(id+"F0.wireOp",EDGE,"E167"),sQuery(id+"F0.wireOp",EDGE,"E168"),sQuery(id+"F0.wireOp",EDGE,"E168"),sQuery(id+"F0.wireOp",EDGE,"E169"),sQuery(id+"F0.wireOp",EDGE,"E170"),sQuery(id+"F0.wireOp",EDGE,"E171"),sQuery(id+"F0.wireOp",EDGE,"E171"),sQuery(id+"F0.wireOp",EDGE,"E171"),sQuery(id+"F0.wireOp",EDGE,"E172"),sQuery(id+"F0.wireOp",EDGE,"E173"),sQuery(id+"F0.wireOp",EDGE,"E174"),sQuery(id+"F0.wireOp",EDGE,"E174"),sQuery(id+"F0.wireOp",EDGE,"E175"),sQuery(id+"F0.wireOp",EDGE,"E176"),sQuery(id+"F0.wireOp",EDGE,"E177"),sQuery(id+"F0.wireOp",EDGE,"E178"),sQuery(id+"F0.wireOp",EDGE,"E179"),sQuery(id+"F0.wireOp",EDGE,"E180"),sQuery(id+"F0.wireOp",EDGE,"a4655eb5-c447-468b-97e3-10430426e770"),sQuery(id+"F0.wireOp",EDGE,"3d21500a-10dd-473c-9b8b-289e5a69b6c9"),sQuery(id+"F0.wireOp",EDGE,"E598")])]});
            var Q1;
            Q1=makeQuery(id+"F1.opExtrude","SWEPT_FACE",FACE,{"disambiguationData":[OSD([sQuery(id+"F0.wireOp",EDGE,"E1")])]});
            circularPattern(context, id + "F2", {"operationType" : NewBodyOperationType.ADD, "entities" : qUnion([Q0]), "axis" : qUnion([Q1]), "angle" : 3.8 * degree, "instanceCount" : round(19)});
        }
        {
            var Q0;
            Q0=makeQuery(id+"F1.opExtrude","SWEPT_BODY",BODY,{"disambiguationData":[OSD([sQuery(id+"F0.wireOp",EDGE,"E6"),sQuery(id+"F0.wireOp",EDGE,"E7"),sQuery(id+"F0.wireOp",EDGE,"E8"),sQuery(id+"F0.wireOp",EDGE,"E9"),sQuery(id+"F0.wireOp",EDGE,"E10"),sQuery(id+"F0.wireOp",EDGE,"E11"),sQuery(id+"F0.wireOp",EDGE,"E11"),sQuery(id+"F0.wireOp",EDGE,"E12"),sQuery(id+"F0.wireOp",EDGE,"E13"),sQuery(id+"F0.wireOp",EDGE,"E14"),sQuery(id+"F0.wireOp",EDGE,"E14"),sQuery(id+"F0.wireOp",EDGE,"E14"),sQuery(id+"F0.wireOp",EDGE,"E15"),sQuery(id+"F0.wireOp",EDGE,"E16"),sQuery(id+"F0.wireOp",EDGE,"E17"),sQuery(id+"F0.wireOp",EDGE,"E17"),sQuery(id+"F0.wireOp",EDGE,"E18"),sQuery(id+"F0.wireOp",EDGE,"E19"),sQuery(id+"F0.wireOp",EDGE,"E20"),sQuery(id+"F0.wireOp",EDGE,"E21"),sQuery(id+"F0.wireOp",EDGE,"E22"),sQuery(id+"F0.wireOp",EDGE,"E23"),sQuery(id+"F0.wireOp",EDGE,"E24"),sQuery(id+"F0.wireOp",EDGE,"E25"),sQuery(id+"F0.wireOp",EDGE,"E26"),sQuery(id+"F0.wireOp",EDGE,"E27"),sQuery(id+"F0.wireOp",EDGE,"E28"),sQuery(id+"F0.wireOp",EDGE,"E29"),sQuery(id+"F0.wireOp",EDGE,"E30"),sQuery(id+"F0.wireOp",EDGE,"E31"),sQuery(id+"F0.wireOp",EDGE,"E32"),sQuery(id+"F0.wireOp",EDGE,"E33"),sQuery(id+"F0.wireOp",EDGE,"E33"),sQuery(id+"F0.wireOp",EDGE,"E33"),sQuery(id+"F0.wireOp",EDGE,"E33"),sQuery(id+"F0.wireOp",EDGE,"E34"),sQuery(id+"F0.wireOp",EDGE,"E35"),sQuery(id+"F0.wireOp",EDGE,"E36"),sQuery(id+"F0.wireOp",EDGE,"E37"),sQuery(id+"F0.wireOp",EDGE,"E38"),sQuery(id+"F0.wireOp",EDGE,"E39"),sQuery(id+"F0.wireOp",EDGE,"E40"),sQuery(id+"F0.wireOp",EDGE,"E41"),sQuery(id+"F0.wireOp",EDGE,"E42"),sQuery(id+"F0.wireOp",EDGE,"E42"),sQuery(id+"F0.wireOp",EDGE,"E43"),sQuery(id+"F0.wireOp",EDGE,"E44"),sQuery(id+"F0.wireOp",EDGE,"E45"),sQuery(id+"F0.wireOp",EDGE,"E46"),sQuery(id+"F0.wireOp",EDGE,"E47"),sQuery(id+"F0.wireOp",EDGE,"E48"),sQuery(id+"F0.wireOp",EDGE,"E49"),sQuery(id+"F0.wireOp",EDGE,"E50"),sQuery(id+"F0.wireOp",EDGE,"E51"),sQuery(id+"F0.wireOp",EDGE,"E52"),sQuery(id+"F0.wireOp",EDGE,"E52"),sQuery(id+"F0.wireOp",EDGE,"E53"),sQuery(id+"F0.wireOp",EDGE,"E54"),sQuery(id+"F0.wireOp",EDGE,"E55"),sQuery(id+"F0.wireOp",EDGE,"E56"),sQuery(id+"F0.wireOp",EDGE,"E57"),sQuery(id+"F0.wireOp",EDGE,"E58"),sQuery(id+"F0.wireOp",EDGE,"E59"),sQuery(id+"F0.wireOp",EDGE,"E60"),sQuery(id+"F0.wireOp",EDGE,"E61"),sQuery(id+"F0.wireOp",EDGE,"E62"),sQuery(id+"F0.wireOp",EDGE,"E63"),sQuery(id+"F0.wireOp",EDGE,"E64"),sQuery(id+"F0.wireOp",EDGE,"E65"),sQuery(id+"F0.wireOp",EDGE,"E66"),sQuery(id+"F0.wireOp",EDGE,"E67"),sQuery(id+"F0.wireOp",EDGE,"E67"),sQuery(id+"F0.wireOp",EDGE,"E68"),sQuery(id+"F0.wireOp",EDGE,"E69"),sQuery(id+"F0.wireOp",EDGE,"E70"),sQuery(id+"F0.wireOp",EDGE,"E71"),sQuery(id+"F0.wireOp",EDGE,"E72"),sQuery(id+"F0.wireOp",EDGE,"E72"),sQuery(id+"F0.wireOp",EDGE,"E72"),sQuery(id+"F0.wireOp",EDGE,"E73"),sQuery(id+"F0.wireOp",EDGE,"E74"),sQuery(id+"F0.wireOp",EDGE,"E75"),sQuery(id+"F0.wireOp",EDGE,"E76"),sQuery(id+"F0.wireOp",EDGE,"E77"),sQuery(id+"F0.wireOp",EDGE,"E78"),sQuery(id+"F0.wireOp",EDGE,"E79"),sQuery(id+"F0.wireOp",EDGE,"E80"),sQuery(id+"F0.wireOp",EDGE,"E81"),sQuery(id+"F0.wireOp",EDGE,"E82"),sQuery(id+"F0.wireOp",EDGE,"E83"),sQuery(id+"F0.wireOp",EDGE,"E84"),sQuery(id+"F0.wireOp",EDGE,"E84"),sQuery(id+"F0.wireOp",EDGE,"E85"),sQuery(id+"F0.wireOp",EDGE,"E86"),sQuery(id+"F0.wireOp",EDGE,"E87"),sQuery(id+"F0.wireOp",EDGE,"E88"),sQuery(id+"F0.wireOp",EDGE,"E89"),sQuery(id+"F0.wireOp",EDGE,"E90"),sQuery(id+"F0.wireOp",EDGE,"E91"),sQuery(id+"F0.wireOp",EDGE,"E92"),sQuery(id+"F0.wireOp",EDGE,"E93"),sQuery(id+"F0.wireOp",EDGE,"E94"),sQuery(id+"F0.wireOp",EDGE,"E95"),sQuery(id+"F0.wireOp",EDGE,"E96"),sQuery(id+"F0.wireOp",EDGE,"E97"),sQuery(id+"F0.wireOp",EDGE,"E98"),sQuery(id+"F0.wireOp",EDGE,"E99"),sQuery(id+"F0.wireOp",EDGE,"E100"),sQuery(id+"F0.wireOp",EDGE,"E101"),sQuery(id+"F0.wireOp",EDGE,"E101"),sQuery(id+"F0.wireOp",EDGE,"E102"),sQuery(id+"F0.wireOp",EDGE,"E103"),sQuery(id+"F0.wireOp",EDGE,"E104"),sQuery(id+"F0.wireOp",EDGE,"E105"),sQuery(id+"F0.wireOp",EDGE,"E106"),sQuery(id+"F0.wireOp",EDGE,"E107"),sQuery(id+"F0.wireOp",EDGE,"E108"),sQuery(id+"F0.wireOp",EDGE,"E109"),sQuery(id+"F0.wireOp",EDGE,"E110"),sQuery(id+"F0.wireOp",EDGE,"E111"),sQuery(id+"F0.wireOp",EDGE,"E112"),sQuery(id+"F0.wireOp",EDGE,"E113"),sQuery(id+"F0.wireOp",EDGE,"E113"),sQuery(id+"F0.wireOp",EDGE,"E113"),sQuery(id+"F0.wireOp",EDGE,"E114"),sQuery(id+"F0.wireOp",EDGE,"E115"),sQuery(id+"F0.wireOp",EDGE,"E116"),sQuery(id+"F0.wireOp",EDGE,"E117"),sQuery(id+"F0.wireOp",EDGE,"E118"),sQuery(id+"F0.wireOp",EDGE,"E118"),sQuery(id+"F0.wireOp",EDGE,"E119"),sQuery(id+"F0.wireOp",EDGE,"E120"),sQuery(id+"F0.wireOp",EDGE,"E121"),sQuery(id+"F0.wireOp",EDGE,"E122"),sQuery(id+"F0.wireOp",EDGE,"E123"),sQuery(id+"F0.wireOp",EDGE,"E124"),sQuery(id+"F0.wireOp",EDGE,"E125"),sQuery(id+"F0.wireOp",EDGE,"E126"),sQuery(id+"F0.wireOp",EDGE,"E127"),sQuery(id+"F0.wireOp",EDGE,"E128"),sQuery(id+"F0.wireOp",EDGE,"E129"),sQuery(id+"F0.wireOp",EDGE,"E130"),sQuery(id+"F0.wireOp",EDGE,"E131"),sQuery(id+"F0.wireOp",EDGE,"E132"),sQuery(id+"F0.wireOp",EDGE,"E133"),sQuery(id+"F0.wireOp",EDGE,"E133"),sQuery(id+"F0.wireOp",EDGE,"E134"),sQuery(id+"F0.wireOp",EDGE,"E135"),sQuery(id+"F0.wireOp",EDGE,"E136"),sQuery(id+"F0.wireOp",EDGE,"E137"),sQuery(id+"F0.wireOp",EDGE,"E138"),sQuery(id+"F0.wireOp",EDGE,"E139"),sQuery(id+"F0.wireOp",EDGE,"E140"),sQuery(id+"F0.wireOp",EDGE,"E141"),sQuery(id+"F0.wireOp",EDGE,"E142"),sQuery(id+"F0.wireOp",EDGE,"E143"),sQuery(id+"F0.wireOp",EDGE,"E143"),sQuery(id+"F0.wireOp",EDGE,"E144"),sQuery(id+"F0.wireOp",EDGE,"E145"),sQuery(id+"F0.wireOp",EDGE,"E146"),sQuery(id+"F0.wireOp",EDGE,"E147"),sQuery(id+"F0.wireOp",EDGE,"E148"),sQuery(id+"F0.wireOp",EDGE,"E149"),sQuery(id+"F0.wireOp",EDGE,"E150"),sQuery(id+"F0.wireOp",EDGE,"E151"),sQuery(id+"F0.wireOp",EDGE,"E152"),sQuery(id+"F0.wireOp",EDGE,"E152"),sQuery(id+"F0.wireOp",EDGE,"E152"),sQuery(id+"F0.wireOp",EDGE,"E152"),sQuery(id+"F0.wireOp",EDGE,"E153"),sQuery(id+"F0.wireOp",EDGE,"E154"),sQuery(id+"F0.wireOp",EDGE,"E155"),sQuery(id+"F0.wireOp",EDGE,"E156"),sQuery(id+"F0.wireOp",EDGE,"E157"),sQuery(id+"F0.wireOp",EDGE,"E158"),sQuery(id+"F0.wireOp",EDGE,"E159"),sQuery(id+"F0.wireOp",EDGE,"E160"),sQuery(id+"F0.wireOp",EDGE,"E161"),sQuery(id+"F0.wireOp",EDGE,"E162"),sQuery(id+"F0.wireOp",EDGE,"E163"),sQuery(id+"F0.wireOp",EDGE,"E164"),sQuery(id+"F0.wireOp",EDGE,"E165"),sQuery(id+"F0.wireOp",EDGE,"E166"),sQuery(id+"F0.wireOp",EDGE,"E167"),sQuery(id+"F0.wireOp",EDGE,"E168"),sQuery(id+"F0.wireOp",EDGE,"E168"),sQuery(id+"F0.wireOp",EDGE,"E169"),sQuery(id+"F0.wireOp",EDGE,"E170"),sQuery(id+"F0.wireOp",EDGE,"E171"),sQuery(id+"F0.wireOp",EDGE,"E171"),sQuery(id+"F0.wireOp",EDGE,"E171"),sQuery(id+"F0.wireOp",EDGE,"E172"),sQuery(id+"F0.wireOp",EDGE,"E173"),sQuery(id+"F0.wireOp",EDGE,"E174"),sQuery(id+"F0.wireOp",EDGE,"E174"),sQuery(id+"F0.wireOp",EDGE,"E175"),sQuery(id+"F0.wireOp",EDGE,"E176"),sQuery(id+"F0.wireOp",EDGE,"E177"),sQuery(id+"F0.wireOp",EDGE,"E178"),sQuery(id+"F0.wireOp",EDGE,"E179"),sQuery(id+"F0.wireOp",EDGE,"E180"),sQuery(id+"F0.wireOp",EDGE,"a4655eb5-c447-468b-97e3-10430426e770"),sQuery(id+"F0.wireOp",EDGE,"3d21500a-10dd-473c-9b8b-289e5a69b6c9"),sQuery(id+"F0.wireOp",EDGE,"E598")])]});
            var Q1;
            Q1=makeQuery(id+"F1.opExtrude","SWEPT_FACE",FACE,{"disambiguationData":[OSD([sQuery(id+"F0.wireOp",EDGE,"E1")])]});
            circularPattern(context, id + "F3", {"entities" : qUnion([Q0]), "axis" : qUnion([Q1]), "angle" : 72 * degree, "instanceCount" : round(5)});
        }
        {
            var Q0;
            {var subQ6=sQuery(id+"F0.wireOp",EDGE,"E6");Q0=makeQuery(id+"F0.imprint","IMPRINT",FACE,{"disambiguationData":[TD([[makeQuery(id+"F0.imprint","IMPRINT",EDGE,{"derivedFrom":subQ6}),-1.0]])]});}
            var Q1;
            {var subQ6=sQuery(id+"F0.wireOp",EDGE,"E423");Q1=makeQuery(id+"F0.imprint","IMPRINT",FACE,{"disambiguationData":[TD([[makeQuery(id+"F0.imprint","IMPRINT",EDGE,{"derivedFrom":subQ6}),1.0]])]});}
            var Q2;
            {var subQ3=sQuery(id+"F0.wireOp",EDGE,"E6");Q2=makeQuery(id+"F0.imprint","IMPRINT",FACE,{"disambiguationData":[TD([[makeQuery(id+"F0.imprint","IMPRINT",EDGE,{"derivedFrom":subQ3}),1.0]])]});}
            var Q3;
            Q3=makeQuery(id+"F0.imprint","IMPRINT",FACE,{"disambiguationData":[TD([[makeQuery(id+"F0.imprint","IMPRINT",EDGE,{"derivedFrom":sQuery(id+"F0.wireOp",EDGE,"E4")}),1.0]])]});
            var Q4;
            Q4=makeQuery(id+"F0.imprint","IMPRINT",FACE,{"disambiguationData":[TD([[makeQuery(id+"F0.imprint","IMPRINT",EDGE,{"derivedFrom":sQuery(id+"F0.wireOp",EDGE,"E5")}),-1.0]])]});
            var Q5;
            Q5=makeQuery(id+"F0.imprint","IMPRINT",FACE,{"disambiguationData":[TD([[makeQuery(id+"F0.imprint","IMPRINT",EDGE,{"derivedFrom":sQuery(id+"F0.wireOp",EDGE,"E4")}),-1.0]])]});
            var Q6;
            {var subQ1=sQuery(id+"F0.wireOp",EDGE,"E600");var subQ6=sQuery(id+"F0.wireOp",EDGE,"E3");var subQ8=makeQuery(id+"F0.imprint","INTERSECT",VERTEX,{"disambiguationData":[OD(0.0)],"derivedFrom":[subQ6,subQ1]});Q6=makeQuery(id+"F0.imprint","IMPRINT",FACE,{"disambiguationData":[TD([[makeQuery(id+"F0.imprint","IMPRINT",EDGE,{"disambiguationData":[TD([[subQ8,-1.0]])],"derivedFrom":subQ6}),-1.0]])]});}
            var Q7;
            {var subQ0=sQuery(id+"F0.wireOp",EDGE,"E602");var subQ1=sQuery(id+"F0.wireOp",EDGE,"E600");var subQ2=makeQuery(id+"F0.imprint","INTERSECT",VERTEX,{"derivedFrom":[subQ1,subQ0]});Q7=makeQuery(id+"F0.imprint","IMPRINT",FACE,{"disambiguationData":[TD([[makeQuery(id+"F0.imprint","IMPRINT",EDGE,{"disambiguationData":[TD([[subQ2,-1.0]])],"derivedFrom":subQ1}),1.0]])]});}
            var Q8;
            {var subQ1=sQuery(id+"F0.wireOp",EDGE,"E600");var subQ3=sQuery(id+"F0.wireOp",EDGE,"E3");var subQ5=makeQuery(id+"F0.imprint","INTERSECT",VERTEX,{"disambiguationData":[OD(1.0)],"derivedFrom":[subQ3,subQ1]});Q8=makeQuery(id+"F0.imprint","IMPRINT",FACE,{"disambiguationData":[TD([[makeQuery(id+"F0.imprint","IMPRINT",EDGE,{"disambiguationData":[TD([[subQ5,-1.0]])],"derivedFrom":subQ3}),-1.0]])]});}
            var Q9;
            {var subQ0=sQuery(id+"F0.wireOp",EDGE,"E602");var subQ3=sQuery(id+"F0.wireOp",EDGE,"E3");var subQ4=makeQuery(id+"F0.imprint","INTERSECT",VERTEX,{"derivedFrom":[subQ3,subQ0]});Q9=makeQuery(id+"F0.imprint","IMPRINT",FACE,{"disambiguationData":[TD([[makeQuery(id+"F0.imprint","IMPRINT",EDGE,{"disambiguationData":[TD([[subQ4,1.0]])],"derivedFrom":subQ3}),-1.0]])]});}
            var Q10;
            {var subQ1=sQuery(id+"F0.wireOp",EDGE,"E600");var subQ3=sQuery(id+"F0.wireOp",EDGE,"E3");var subQ5=makeQuery(id+"F0.imprint","INTERSECT",VERTEX,{"disambiguationData":[OD(0.0)],"derivedFrom":[subQ3,subQ1]});Q10=makeQuery(id+"F0.imprint","IMPRINT",FACE,{"disambiguationData":[TD([[makeQuery(id+"F0.imprint","IMPRINT",EDGE,{"disambiguationData":[TD([[subQ5,1.0]])],"derivedFrom":subQ3}),-1.0]])]});}
            extrude(context, id + "F4", {"entities" : qUnion([Q0, Q1, Q2, Q3, Q4, Q5, Q6, Q7, Q8, Q9, Q10]), "oppositeDirection" : true, "depth" : 1 * mm});
        }
    });
